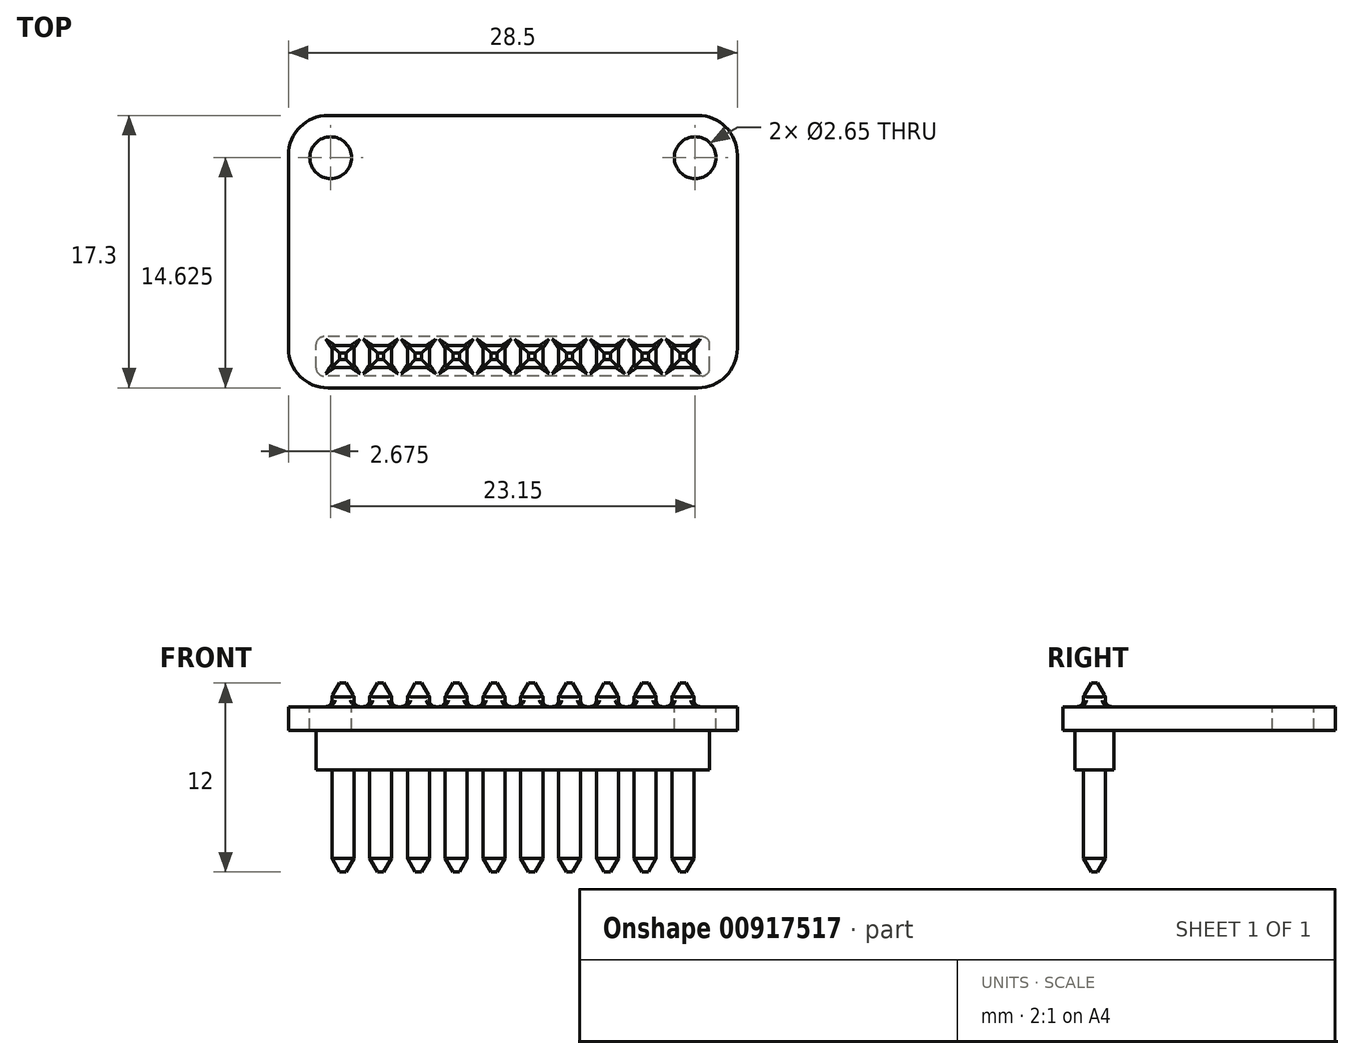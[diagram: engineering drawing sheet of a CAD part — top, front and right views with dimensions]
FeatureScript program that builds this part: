
annotation { "Feature Type Name" : "Feature", "Feature Type Description" : "" }
export const myFeature = defineFeature(function(context is Context, id is Id, definition is map)
    precondition{}
    {
        {
            var Q0;
            Q0=qCreatedBy(makeId("Top.planeOp"),FACE);
            var sketch = newSketch(context, id + "F0", { "sketchPlane" : qUnion([Q0])});
            skLineSegment(sketch, "E0.bottom", {"start": v(14.25, 8.65) * mm, "end": v(-14.25, 8.65) * mm});
            skLineSegment(sketch, "E0.top", {"start": v(14.25, -8.65) * mm, "end": v(-14.25, -8.65) * mm});
            skLineSegment(sketch, "E0.left", {"start": v(14.25, 8.65) * mm, "end": v(14.25, -8.65) * mm});
            skLineSegment(sketch, "E0.right", {"start": v(-14.25, 8.65) * mm, "end": v(-14.25, -8.65) * mm});
            skPoint(sketch, "E0.middle", {"position": v(0, 0) * mm});
            skCircle(sketch, "E1", {"center": v(-11.58, 5.97) * mm, "radius": 1.32 * mm, "construction": true});
            skLineSegment(sketch, "E2", {"start": v(0, 8.65) * mm, "end": v(0, -8.65) * mm, "construction": true});
            skCircle(sketch, "E3.MirrorC", {"center": v(11.57, 5.97) * mm, "radius": 1.32 * mm, "construction": true});
            skCircle(sketch, "E4", {"center": v(-11.58, 5.97) * mm, "radius": 1.82 * mm});
            skCircle(sketch, "E5", {"center": v(11.57, 5.97) * mm, "radius": 1.82 * mm});
            skSolve(sketch);
        }
        {
            var Q0;
            Q0 = qSketchRegion(id + "F0", true);
            extrude(context, id + "F1", {"entities" : qUnion([Q0]), "depth" : 1.5 * mm, "offsetDistance" : 25 * mm});
        }
        {
            var Q0;
            Q0=makeQuery(id+"F1.opExtrude","SWEPT_EDGE",EDGE,{"disambiguationData":[OSD([sQuery(id+"F0.wireOp",EDGE,"E0.bottom"),sQuery(id+"F0.wireOp",EDGE,"E0.left")])]});
            var Q1;
            Q1=makeQuery(id+"F1.opExtrude","SWEPT_EDGE",EDGE,{"disambiguationData":[OSD([sQuery(id+"F0.wireOp",EDGE,"E0.bottom"),sQuery(id+"F0.wireOp",EDGE,"E0.right")])]});
            var Q2;
            Q2=makeQuery(id+"F1.opExtrude","SWEPT_EDGE",EDGE,{"disambiguationData":[OSD([sQuery(id+"F0.wireOp",EDGE,"E0.top"),sQuery(id+"F0.wireOp",EDGE,"E0.right")])]});
            var Q3;
            Q3=makeQuery(id+"F1.opExtrude","SWEPT_EDGE",EDGE,{"disambiguationData":[OSD([sQuery(id+"F0.wireOp",EDGE,"E0.top"),sQuery(id+"F0.wireOp",EDGE,"E0.left")])]});
            fillet(context, id + "F2", {"entities" : qUnion([Q0, Q1, Q2, Q3]), "radius" : 2.5 * mm, "tangentPropagation" : true, "allowEdgeOverflow" : false});
        }
        {
            var Q0;
            Q0=makeQuery(id+"F1.opExtrude","CAP_FACE",FACE,{"disambiguationData":[OSD([sQuery(id+"F0.wireOp",EDGE,"E0.bottom"),sQuery(id+"F0.wireOp",EDGE,"E0.top"),sQuery(id+"F0.wireOp",EDGE,"E0.left"),sQuery(id+"F0.wireOp",EDGE,"E0.right"),sQuery(id+"F0.wireOp",EDGE,"E4"),sQuery(id+"F0.wireOp",EDGE,"E5")])],"isStart":false});
            var sketch = newSketch(context, id + "F3", { "sketchPlane" : qUnion([Q0])});
            skCircle(sketch, "E6.0", {"center": v(-11.58, 5.97) * mm, "radius": 1.83 * mm});
            skCircle(sketch, "E6.1", {"center": v(11.57, 5.97) * mm, "radius": 1.83 * mm});
            skCircle(sketch, "E7", {"center": v(-11.58, 5.97) * mm, "radius": 1.32 * mm});
            skCircle(sketch, "E8", {"center": v(11.57, 5.97) * mm, "radius": 1.32 * mm});
            skSolve(sketch);
        }
        {
            var Q0;
            Q0 = qSketchRegion(id + "F3", true);
            extrude(context, id + "F4", {"entities" : qUnion([Q0]), "operationType" : NewBodyOperationType.ADD, "oppositeDirection" : true, "depth" : 1.5 * mm, "offsetDistance" : 25 * mm});
        }
        {
            var Q0;
            Q0=makeQuery(id+"F1.opExtrude","CAP_FACE",FACE,{"disambiguationData":[OSD([sQuery(id+"F0.wireOp",EDGE,"E0.bottom"),sQuery(id+"F0.wireOp",EDGE,"E0.top"),sQuery(id+"F0.wireOp",EDGE,"E0.left"),sQuery(id+"F0.wireOp",EDGE,"E0.right"),sQuery(id+"F0.wireOp",EDGE,"E4"),sQuery(id+"F0.wireOp",EDGE,"E5")])],"isStart":true});
            var sketch = newSketch(context, id + "F5", { "sketchPlane" : qUnion([Q0])});
            skLineSegment(sketch, "E9.bottom", {"start": v(12.5, 7.9) * mm, "end": v(-12.5, 7.9) * mm});
            skLineSegment(sketch, "E9.top", {"start": v(12.5, 5.4) * mm, "end": v(-12.5, 5.4) * mm});
            skLineSegment(sketch, "E9.left", {"start": v(12.5, 7.9) * mm, "end": v(12.5, 5.4) * mm});
            skLineSegment(sketch, "E9.right", {"start": v(-12.5, 7.9) * mm, "end": v(-12.5, 5.4) * mm});
            skPoint(sketch, "E9.middle", {"position": v(0, 6.65) * mm});
            skSolve(sketch);
        }
        {
            var Q0;
            Q0 = qSketchRegion(id + "F5", true);
            extrude(context, id + "F6", {"entities" : qUnion([Q0]), "depth" : 2.5 * mm, "offsetDistance" : 25 * mm});
        }
        {
            var Q0;
            Q0=makeQuery(id+"F6.opExtrude","SWEPT_EDGE",EDGE,{"disambiguationData":[OSD([sQuery(id+"F5.wireOp",EDGE,"E9.bottom"),sQuery(id+"F5.wireOp",EDGE,"E9.left")])]});
            var Q1;
            Q1=makeQuery(id+"F6.opExtrude","SWEPT_EDGE",EDGE,{"disambiguationData":[OSD([sQuery(id+"F5.wireOp",EDGE,"E9.bottom"),sQuery(id+"F5.wireOp",EDGE,"E9.right")])]});
            var Q2;
            Q2=makeQuery(id+"F6.opExtrude","SWEPT_EDGE",EDGE,{"disambiguationData":[OSD([sQuery(id+"F5.wireOp",EDGE,"E9.top"),sQuery(id+"F5.wireOp",EDGE,"E9.right")])]});
            var Q3;
            Q3=makeQuery(id+"F6.opExtrude","SWEPT_EDGE",EDGE,{"disambiguationData":[OSD([sQuery(id+"F5.wireOp",EDGE,"E9.top"),sQuery(id+"F5.wireOp",EDGE,"E9.left")])]});
            fillet(context, id + "F7", {"entities" : qUnion([Q0, Q1, Q2, Q3]), "radius" : 0.5 * mm, "tangentPropagation" : true, "allowEdgeOverflow" : false});
        }
        {
            var Q0;
            Q0=makeQuery(id+"F6.opExtrude","CAP_FACE",FACE,{"disambiguationData":[OSD([sQuery(id+"F5.wireOp",EDGE,"E9.bottom"),sQuery(id+"F5.wireOp",EDGE,"E9.top"),sQuery(id+"F5.wireOp",EDGE,"E9.left"),sQuery(id+"F5.wireOp",EDGE,"E9.right")])],"isStart":false});
            var sketch = newSketch(context, id + "F8", { "sketchPlane" : qUnion([Q0])});
            skLineSegment(sketch, "E10.bottom", {"start": v(-10.1, 7.35) * mm, "end": v(-11.5, 7.35) * mm});
            skLineSegment(sketch, "E10.top", {"start": v(-10.1, 5.95) * mm, "end": v(-11.5, 5.95) * mm});
            skLineSegment(sketch, "E10.left", {"start": v(-10.1, 7.35) * mm, "end": v(-10.1, 5.95) * mm});
            skLineSegment(sketch, "E10.right", {"start": v(-11.5, 7.35) * mm, "end": v(-11.5, 5.95) * mm});
            skPoint(sketch, "E10.middle", {"position": v(-10.8, 6.65) * mm});
            skPoint(sketch, "E10.middle.positionSnap0", {"position": v(-12.5, 6.65) * mm});
            skPoint(sketch, "E10.centerSnap0", {"position": v(-12.5, 6.65) * mm});
            skLineSegment(sketch, "E11.1.0.0", {"start": v(-7.7, 7.35) * mm, "end": v(-7.7, 5.95) * mm});
            skLineSegment(sketch, "E11.1.0.1", {"start": v(-9.1, 7.35) * mm, "end": v(-9.1, 5.95) * mm});
            skLineSegment(sketch, "E11.1.0.2", {"start": v(-7.7, 5.95) * mm, "end": v(-9.1, 5.95) * mm});
            skPoint(sketch, "E11.1.0.3", {"position": v(-10.1, 6.65) * mm});
            skLineSegment(sketch, "E11.1.0.4", {"start": v(-7.7, 7.35) * mm, "end": v(-9.1, 7.35) * mm});
            skPoint(sketch, "E11.1.0.5", {"position": v(-8.4, 6.65) * mm});
            skPoint(sketch, "E11.1.0.6", {"position": v(-10.1, 6.65) * mm});
            skLineSegment(sketch, "E11.2.0.0", {"start": v(-5.3, 7.35) * mm, "end": v(-5.3, 5.95) * mm});
            skLineSegment(sketch, "E11.2.0.1", {"start": v(-6.7, 7.35) * mm, "end": v(-6.7, 5.95) * mm});
            skLineSegment(sketch, "E11.2.0.2", {"start": v(-5.3, 5.95) * mm, "end": v(-6.7, 5.95) * mm});
            skPoint(sketch, "E11.2.0.3", {"position": v(-7.7, 6.65) * mm});
            skLineSegment(sketch, "E11.2.0.4", {"start": v(-5.3, 7.35) * mm, "end": v(-6.7, 7.35) * mm});
            skPoint(sketch, "E11.2.0.5", {"position": v(-6, 6.65) * mm});
            skPoint(sketch, "E11.2.0.6", {"position": v(-7.7, 6.65) * mm});
            skLineSegment(sketch, "E11.3.0.0", {"start": v(-2.9, 7.35) * mm, "end": v(-2.9, 5.95) * mm});
            skLineSegment(sketch, "E11.3.0.1", {"start": v(-4.3, 7.35) * mm, "end": v(-4.3, 5.95) * mm});
            skLineSegment(sketch, "E11.3.0.2", {"start": v(-2.9, 5.95) * mm, "end": v(-4.3, 5.95) * mm});
            skPoint(sketch, "E11.3.0.3", {"position": v(-5.3, 6.65) * mm});
            skLineSegment(sketch, "E11.3.0.4", {"start": v(-2.9, 7.35) * mm, "end": v(-4.3, 7.35) * mm});
            skPoint(sketch, "E11.3.0.5", {"position": v(-3.6, 6.65) * mm});
            skPoint(sketch, "E11.3.0.6", {"position": v(-5.3, 6.65) * mm});
            skLineSegment(sketch, "E11.4.0.0", {"start": v(-0.5, 7.35) * mm, "end": v(-0.5, 5.95) * mm});
            skLineSegment(sketch, "E11.4.0.1", {"start": v(-1.9, 7.35) * mm, "end": v(-1.9, 5.95) * mm});
            skLineSegment(sketch, "E11.4.0.2", {"start": v(-0.5, 5.95) * mm, "end": v(-1.9, 5.95) * mm});
            skPoint(sketch, "E11.4.0.3", {"position": v(-2.9, 6.65) * mm});
            skLineSegment(sketch, "E11.4.0.4", {"start": v(-0.5, 7.35) * mm, "end": v(-1.9, 7.35) * mm});
            skPoint(sketch, "E11.4.0.5", {"position": v(-1.2, 6.65) * mm});
            skPoint(sketch, "E11.4.0.6", {"position": v(-2.9, 6.65) * mm});
            skLineSegment(sketch, "E11.5.0.0", {"start": v(1.9, 7.35) * mm, "end": v(1.9, 5.95) * mm});
            skLineSegment(sketch, "E11.5.0.1", {"start": v(0.5, 7.35) * mm, "end": v(0.5, 5.95) * mm});
            skLineSegment(sketch, "E11.5.0.2", {"start": v(1.9, 5.95) * mm, "end": v(0.5, 5.95) * mm});
            skPoint(sketch, "E11.5.0.3", {"position": v(-0.5, 6.65) * mm});
            skLineSegment(sketch, "E11.5.0.4", {"start": v(1.9, 7.35) * mm, "end": v(0.5, 7.35) * mm});
            skPoint(sketch, "E11.5.0.5", {"position": v(1.2, 6.65) * mm});
            skPoint(sketch, "E11.5.0.6", {"position": v(-0.5, 6.65) * mm});
            skLineSegment(sketch, "E11.6.0.0", {"start": v(4.3, 7.35) * mm, "end": v(4.3, 5.95) * mm});
            skLineSegment(sketch, "E11.6.0.1", {"start": v(2.9, 7.35) * mm, "end": v(2.9, 5.95) * mm});
            skLineSegment(sketch, "E11.6.0.2", {"start": v(4.3, 5.95) * mm, "end": v(2.9, 5.95) * mm});
            skPoint(sketch, "E11.6.0.3", {"position": v(1.9, 6.65) * mm});
            skLineSegment(sketch, "E11.6.0.4", {"start": v(4.3, 7.35) * mm, "end": v(2.9, 7.35) * mm});
            skPoint(sketch, "E11.6.0.5", {"position": v(3.6, 6.65) * mm});
            skPoint(sketch, "E11.6.0.6", {"position": v(1.9, 6.65) * mm});
            skLineSegment(sketch, "E11.7.0.0", {"start": v(6.7, 7.35) * mm, "end": v(6.7, 5.95) * mm});
            skLineSegment(sketch, "E11.7.0.1", {"start": v(5.3, 7.35) * mm, "end": v(5.3, 5.95) * mm});
            skLineSegment(sketch, "E11.7.0.2", {"start": v(6.7, 5.95) * mm, "end": v(5.3, 5.95) * mm});
            skPoint(sketch, "E11.7.0.3", {"position": v(4.3, 6.65) * mm});
            skLineSegment(sketch, "E11.7.0.4", {"start": v(6.7, 7.35) * mm, "end": v(5.3, 7.35) * mm});
            skPoint(sketch, "E11.7.0.5", {"position": v(6, 6.65) * mm});
            skPoint(sketch, "E11.7.0.6", {"position": v(4.3, 6.65) * mm});
            skLineSegment(sketch, "E11.8.0.0", {"start": v(9.1, 7.35) * mm, "end": v(9.1, 5.95) * mm});
            skLineSegment(sketch, "E11.8.0.1", {"start": v(7.7, 7.35) * mm, "end": v(7.7, 5.95) * mm});
            skLineSegment(sketch, "E11.8.0.2", {"start": v(9.1, 5.95) * mm, "end": v(7.7, 5.95) * mm});
            skPoint(sketch, "E11.8.0.3", {"position": v(6.7, 6.65) * mm});
            skLineSegment(sketch, "E11.8.0.4", {"start": v(9.1, 7.35) * mm, "end": v(7.7, 7.35) * mm});
            skPoint(sketch, "E11.8.0.5", {"position": v(8.4, 6.65) * mm});
            skPoint(sketch, "E11.8.0.6", {"position": v(6.7, 6.65) * mm});
            skLineSegment(sketch, "E11.9.0.0", {"start": v(11.5, 7.35) * mm, "end": v(11.5, 5.95) * mm});
            skLineSegment(sketch, "E11.9.0.1", {"start": v(10.1, 7.35) * mm, "end": v(10.1, 5.95) * mm});
            skLineSegment(sketch, "E11.9.0.2", {"start": v(11.5, 5.95) * mm, "end": v(10.1, 5.95) * mm});
            skPoint(sketch, "E11.9.0.3", {"position": v(9.1, 6.65) * mm});
            skLineSegment(sketch, "E11.9.0.4", {"start": v(11.5, 7.35) * mm, "end": v(10.1, 7.35) * mm});
            skPoint(sketch, "E11.9.0.5", {"position": v(10.8, 6.65) * mm});
            skPoint(sketch, "E11.9.0.6", {"position": v(9.1, 6.65) * mm});
            skLineSegment(sketch, "E11.direction1", {"start": v(-12.5, 6.65) * mm, "end": v(-10.1, 6.65) * mm, "construction": true});
            skSolve(sketch);
        }
        {
            var Q0;
            Q0 = qSketchRegion(id + "F8", true);
            extrude(context, id + "F9", {"entities" : qUnion([Q0]), "operationType" : NewBodyOperationType.ADD, "depth" : 6.5 * mm, "offsetDistance" : 25 * mm, "hasSecondDirection" : true, "secondDirectionOppositeDirection" : true, "secondDirectionDepth" : 5.5 * mm});
        }
        {
            var Q0;
            Q0=makeQuery(id+"F9.boolean.opBoolean","INTERSECT",EDGE,{"derivedFrom":[makeQuery(id+"F4.boolean.opBoolean","MERGE",FACE,{"derivedFrom":[makeQuery(id+"F1.opExtrude","CAP_FACE",FACE,{"disambiguationData":[OSD([sQuery(id+"F0.wireOp",EDGE,"E0.bottom"),sQuery(id+"F0.wireOp",EDGE,"E0.top"),sQuery(id+"F0.wireOp",EDGE,"E0.left"),sQuery(id+"F0.wireOp",EDGE,"E0.right"),sQuery(id+"F0.wireOp",EDGE,"E4"),sQuery(id+"F0.wireOp",EDGE,"E5")])],"isStart":false}),makeQuery(id+"F4.opExtrude","CAP_FACE",FACE,{"disambiguationData":[OSD([sQuery(id+"F3.wireOp",EDGE,"E6.0"),sQuery(id+"F3.wireOp",EDGE,"E7")])],"isStart":true}),makeQuery(id+"F4.opExtrude","CAP_FACE",FACE,{"disambiguationData":[OSD([sQuery(id+"F3.wireOp",EDGE,"E6.1"),sQuery(id+"F3.wireOp",EDGE,"E8")])],"isStart":true})]}),makeQuery(id+"F9.opExtrude","SWEPT_FACE",FACE,{"disambiguationData":[OSD([sQuery(id+"F8.wireOp",EDGE,"E11.9.0.0")])]})]});
            var Q1;
            Q1=makeQuery(id+"F9.boolean.opBoolean","INTERSECT",EDGE,{"derivedFrom":[makeQuery(id+"F4.boolean.opBoolean","MERGE",FACE,{"derivedFrom":[makeQuery(id+"F1.opExtrude","CAP_FACE",FACE,{"disambiguationData":[OSD([sQuery(id+"F0.wireOp",EDGE,"E0.bottom"),sQuery(id+"F0.wireOp",EDGE,"E0.top"),sQuery(id+"F0.wireOp",EDGE,"E0.left"),sQuery(id+"F0.wireOp",EDGE,"E0.right"),sQuery(id+"F0.wireOp",EDGE,"E4"),sQuery(id+"F0.wireOp",EDGE,"E5")])],"isStart":false}),makeQuery(id+"F4.opExtrude","CAP_FACE",FACE,{"disambiguationData":[OSD([sQuery(id+"F3.wireOp",EDGE,"E6.0"),sQuery(id+"F3.wireOp",EDGE,"E7")])],"isStart":true}),makeQuery(id+"F4.opExtrude","CAP_FACE",FACE,{"disambiguationData":[OSD([sQuery(id+"F3.wireOp",EDGE,"E6.1"),sQuery(id+"F3.wireOp",EDGE,"E8")])],"isStart":true})]}),makeQuery(id+"F9.opExtrude","SWEPT_FACE",FACE,{"disambiguationData":[OSD([sQuery(id+"F8.wireOp",EDGE,"E11.9.0.4")])]})]});
            var Q2;
            Q2=makeQuery(id+"F9.boolean.opBoolean","INTERSECT",EDGE,{"derivedFrom":[makeQuery(id+"F4.boolean.opBoolean","MERGE",FACE,{"derivedFrom":[makeQuery(id+"F1.opExtrude","CAP_FACE",FACE,{"disambiguationData":[OSD([sQuery(id+"F0.wireOp",EDGE,"E0.bottom"),sQuery(id+"F0.wireOp",EDGE,"E0.top"),sQuery(id+"F0.wireOp",EDGE,"E0.left"),sQuery(id+"F0.wireOp",EDGE,"E0.right"),sQuery(id+"F0.wireOp",EDGE,"E4"),sQuery(id+"F0.wireOp",EDGE,"E5")])],"isStart":false}),makeQuery(id+"F4.opExtrude","CAP_FACE",FACE,{"disambiguationData":[OSD([sQuery(id+"F3.wireOp",EDGE,"E6.0"),sQuery(id+"F3.wireOp",EDGE,"E7")])],"isStart":true}),makeQuery(id+"F4.opExtrude","CAP_FACE",FACE,{"disambiguationData":[OSD([sQuery(id+"F3.wireOp",EDGE,"E6.1"),sQuery(id+"F3.wireOp",EDGE,"E8")])],"isStart":true})]}),makeQuery(id+"F9.opExtrude","SWEPT_FACE",FACE,{"disambiguationData":[OSD([sQuery(id+"F8.wireOp",EDGE,"E11.9.0.2")])]})]});
            var Q3;
            Q3=makeQuery(id+"F9.boolean.opBoolean","INTERSECT",EDGE,{"derivedFrom":[makeQuery(id+"F4.boolean.opBoolean","MERGE",FACE,{"derivedFrom":[makeQuery(id+"F1.opExtrude","CAP_FACE",FACE,{"disambiguationData":[OSD([sQuery(id+"F0.wireOp",EDGE,"E0.bottom"),sQuery(id+"F0.wireOp",EDGE,"E0.top"),sQuery(id+"F0.wireOp",EDGE,"E0.left"),sQuery(id+"F0.wireOp",EDGE,"E0.right"),sQuery(id+"F0.wireOp",EDGE,"E4"),sQuery(id+"F0.wireOp",EDGE,"E5")])],"isStart":false}),makeQuery(id+"F4.opExtrude","CAP_FACE",FACE,{"disambiguationData":[OSD([sQuery(id+"F3.wireOp",EDGE,"E6.0"),sQuery(id+"F3.wireOp",EDGE,"E7")])],"isStart":true}),makeQuery(id+"F4.opExtrude","CAP_FACE",FACE,{"disambiguationData":[OSD([sQuery(id+"F3.wireOp",EDGE,"E6.1"),sQuery(id+"F3.wireOp",EDGE,"E8")])],"isStart":true})]}),makeQuery(id+"F9.opExtrude","SWEPT_FACE",FACE,{"disambiguationData":[OSD([sQuery(id+"F8.wireOp",EDGE,"E11.9.0.1")])]})]});
            var Q4;
            Q4=makeQuery(id+"F9.boolean.opBoolean","INTERSECT",EDGE,{"derivedFrom":[makeQuery(id+"F4.boolean.opBoolean","MERGE",FACE,{"derivedFrom":[makeQuery(id+"F1.opExtrude","CAP_FACE",FACE,{"disambiguationData":[OSD([sQuery(id+"F0.wireOp",EDGE,"E0.bottom"),sQuery(id+"F0.wireOp",EDGE,"E0.top"),sQuery(id+"F0.wireOp",EDGE,"E0.left"),sQuery(id+"F0.wireOp",EDGE,"E0.right"),sQuery(id+"F0.wireOp",EDGE,"E4"),sQuery(id+"F0.wireOp",EDGE,"E5")])],"isStart":false}),makeQuery(id+"F4.opExtrude","CAP_FACE",FACE,{"disambiguationData":[OSD([sQuery(id+"F3.wireOp",EDGE,"E6.0"),sQuery(id+"F3.wireOp",EDGE,"E7")])],"isStart":true}),makeQuery(id+"F4.opExtrude","CAP_FACE",FACE,{"disambiguationData":[OSD([sQuery(id+"F3.wireOp",EDGE,"E6.1"),sQuery(id+"F3.wireOp",EDGE,"E8")])],"isStart":true})]}),makeQuery(id+"F9.opExtrude","SWEPT_FACE",FACE,{"disambiguationData":[OSD([sQuery(id+"F8.wireOp",EDGE,"E11.8.0.4")])]})]});
            var Q5;
            Q5=makeQuery(id+"F9.boolean.opBoolean","INTERSECT",EDGE,{"derivedFrom":[makeQuery(id+"F4.boolean.opBoolean","MERGE",FACE,{"derivedFrom":[makeQuery(id+"F1.opExtrude","CAP_FACE",FACE,{"disambiguationData":[OSD([sQuery(id+"F0.wireOp",EDGE,"E0.bottom"),sQuery(id+"F0.wireOp",EDGE,"E0.top"),sQuery(id+"F0.wireOp",EDGE,"E0.left"),sQuery(id+"F0.wireOp",EDGE,"E0.right"),sQuery(id+"F0.wireOp",EDGE,"E4"),sQuery(id+"F0.wireOp",EDGE,"E5")])],"isStart":false}),makeQuery(id+"F4.opExtrude","CAP_FACE",FACE,{"disambiguationData":[OSD([sQuery(id+"F3.wireOp",EDGE,"E6.0"),sQuery(id+"F3.wireOp",EDGE,"E7")])],"isStart":true}),makeQuery(id+"F4.opExtrude","CAP_FACE",FACE,{"disambiguationData":[OSD([sQuery(id+"F3.wireOp",EDGE,"E6.1"),sQuery(id+"F3.wireOp",EDGE,"E8")])],"isStart":true})]}),makeQuery(id+"F9.opExtrude","SWEPT_FACE",FACE,{"disambiguationData":[OSD([sQuery(id+"F8.wireOp",EDGE,"E11.8.0.0")])]})]});
            var Q6;
            Q6=makeQuery(id+"F9.boolean.opBoolean","INTERSECT",EDGE,{"derivedFrom":[makeQuery(id+"F4.boolean.opBoolean","MERGE",FACE,{"derivedFrom":[makeQuery(id+"F1.opExtrude","CAP_FACE",FACE,{"disambiguationData":[OSD([sQuery(id+"F0.wireOp",EDGE,"E0.bottom"),sQuery(id+"F0.wireOp",EDGE,"E0.top"),sQuery(id+"F0.wireOp",EDGE,"E0.left"),sQuery(id+"F0.wireOp",EDGE,"E0.right"),sQuery(id+"F0.wireOp",EDGE,"E4"),sQuery(id+"F0.wireOp",EDGE,"E5")])],"isStart":false}),makeQuery(id+"F4.opExtrude","CAP_FACE",FACE,{"disambiguationData":[OSD([sQuery(id+"F3.wireOp",EDGE,"E6.0"),sQuery(id+"F3.wireOp",EDGE,"E7")])],"isStart":true}),makeQuery(id+"F4.opExtrude","CAP_FACE",FACE,{"disambiguationData":[OSD([sQuery(id+"F3.wireOp",EDGE,"E6.1"),sQuery(id+"F3.wireOp",EDGE,"E8")])],"isStart":true})]}),makeQuery(id+"F9.opExtrude","SWEPT_FACE",FACE,{"disambiguationData":[OSD([sQuery(id+"F8.wireOp",EDGE,"E11.8.0.2")])]})]});
            var Q7;
            Q7=makeQuery(id+"F9.boolean.opBoolean","INTERSECT",EDGE,{"derivedFrom":[makeQuery(id+"F4.boolean.opBoolean","MERGE",FACE,{"derivedFrom":[makeQuery(id+"F1.opExtrude","CAP_FACE",FACE,{"disambiguationData":[OSD([sQuery(id+"F0.wireOp",EDGE,"E0.bottom"),sQuery(id+"F0.wireOp",EDGE,"E0.top"),sQuery(id+"F0.wireOp",EDGE,"E0.left"),sQuery(id+"F0.wireOp",EDGE,"E0.right"),sQuery(id+"F0.wireOp",EDGE,"E4"),sQuery(id+"F0.wireOp",EDGE,"E5")])],"isStart":false}),makeQuery(id+"F4.opExtrude","CAP_FACE",FACE,{"disambiguationData":[OSD([sQuery(id+"F3.wireOp",EDGE,"E6.0"),sQuery(id+"F3.wireOp",EDGE,"E7")])],"isStart":true}),makeQuery(id+"F4.opExtrude","CAP_FACE",FACE,{"disambiguationData":[OSD([sQuery(id+"F3.wireOp",EDGE,"E6.1"),sQuery(id+"F3.wireOp",EDGE,"E8")])],"isStart":true})]}),makeQuery(id+"F9.opExtrude","SWEPT_FACE",FACE,{"disambiguationData":[OSD([sQuery(id+"F8.wireOp",EDGE,"E11.8.0.1")])]})]});
            var Q8;
            Q8=makeQuery(id+"F9.boolean.opBoolean","INTERSECT",EDGE,{"derivedFrom":[makeQuery(id+"F4.boolean.opBoolean","MERGE",FACE,{"derivedFrom":[makeQuery(id+"F1.opExtrude","CAP_FACE",FACE,{"disambiguationData":[OSD([sQuery(id+"F0.wireOp",EDGE,"E0.bottom"),sQuery(id+"F0.wireOp",EDGE,"E0.top"),sQuery(id+"F0.wireOp",EDGE,"E0.left"),sQuery(id+"F0.wireOp",EDGE,"E0.right"),sQuery(id+"F0.wireOp",EDGE,"E4"),sQuery(id+"F0.wireOp",EDGE,"E5")])],"isStart":false}),makeQuery(id+"F4.opExtrude","CAP_FACE",FACE,{"disambiguationData":[OSD([sQuery(id+"F3.wireOp",EDGE,"E6.0"),sQuery(id+"F3.wireOp",EDGE,"E7")])],"isStart":true}),makeQuery(id+"F4.opExtrude","CAP_FACE",FACE,{"disambiguationData":[OSD([sQuery(id+"F3.wireOp",EDGE,"E6.1"),sQuery(id+"F3.wireOp",EDGE,"E8")])],"isStart":true})]}),makeQuery(id+"F9.opExtrude","SWEPT_FACE",FACE,{"disambiguationData":[OSD([sQuery(id+"F8.wireOp",EDGE,"E11.7.0.0")])]})]});
            var Q9;
            Q9=makeQuery(id+"F9.boolean.opBoolean","INTERSECT",EDGE,{"derivedFrom":[makeQuery(id+"F4.boolean.opBoolean","MERGE",FACE,{"derivedFrom":[makeQuery(id+"F1.opExtrude","CAP_FACE",FACE,{"disambiguationData":[OSD([sQuery(id+"F0.wireOp",EDGE,"E0.bottom"),sQuery(id+"F0.wireOp",EDGE,"E0.top"),sQuery(id+"F0.wireOp",EDGE,"E0.left"),sQuery(id+"F0.wireOp",EDGE,"E0.right"),sQuery(id+"F0.wireOp",EDGE,"E4"),sQuery(id+"F0.wireOp",EDGE,"E5")])],"isStart":false}),makeQuery(id+"F4.opExtrude","CAP_FACE",FACE,{"disambiguationData":[OSD([sQuery(id+"F3.wireOp",EDGE,"E6.0"),sQuery(id+"F3.wireOp",EDGE,"E7")])],"isStart":true}),makeQuery(id+"F4.opExtrude","CAP_FACE",FACE,{"disambiguationData":[OSD([sQuery(id+"F3.wireOp",EDGE,"E6.1"),sQuery(id+"F3.wireOp",EDGE,"E8")])],"isStart":true})]}),makeQuery(id+"F9.opExtrude","SWEPT_FACE",FACE,{"disambiguationData":[OSD([sQuery(id+"F8.wireOp",EDGE,"E11.7.0.4")])]})]});
            var Q10;
            Q10=makeQuery(id+"F9.boolean.opBoolean","INTERSECT",EDGE,{"derivedFrom":[makeQuery(id+"F4.boolean.opBoolean","MERGE",FACE,{"derivedFrom":[makeQuery(id+"F1.opExtrude","CAP_FACE",FACE,{"disambiguationData":[OSD([sQuery(id+"F0.wireOp",EDGE,"E0.bottom"),sQuery(id+"F0.wireOp",EDGE,"E0.top"),sQuery(id+"F0.wireOp",EDGE,"E0.left"),sQuery(id+"F0.wireOp",EDGE,"E0.right"),sQuery(id+"F0.wireOp",EDGE,"E4"),sQuery(id+"F0.wireOp",EDGE,"E5")])],"isStart":false}),makeQuery(id+"F4.opExtrude","CAP_FACE",FACE,{"disambiguationData":[OSD([sQuery(id+"F3.wireOp",EDGE,"E6.0"),sQuery(id+"F3.wireOp",EDGE,"E7")])],"isStart":true}),makeQuery(id+"F4.opExtrude","CAP_FACE",FACE,{"disambiguationData":[OSD([sQuery(id+"F3.wireOp",EDGE,"E6.1"),sQuery(id+"F3.wireOp",EDGE,"E8")])],"isStart":true})]}),makeQuery(id+"F9.opExtrude","SWEPT_FACE",FACE,{"disambiguationData":[OSD([sQuery(id+"F8.wireOp",EDGE,"E11.7.0.2")])]})]});
            var Q11;
            Q11=makeQuery(id+"F9.boolean.opBoolean","INTERSECT",EDGE,{"derivedFrom":[makeQuery(id+"F4.boolean.opBoolean","MERGE",FACE,{"derivedFrom":[makeQuery(id+"F1.opExtrude","CAP_FACE",FACE,{"disambiguationData":[OSD([sQuery(id+"F0.wireOp",EDGE,"E0.bottom"),sQuery(id+"F0.wireOp",EDGE,"E0.top"),sQuery(id+"F0.wireOp",EDGE,"E0.left"),sQuery(id+"F0.wireOp",EDGE,"E0.right"),sQuery(id+"F0.wireOp",EDGE,"E4"),sQuery(id+"F0.wireOp",EDGE,"E5")])],"isStart":false}),makeQuery(id+"F4.opExtrude","CAP_FACE",FACE,{"disambiguationData":[OSD([sQuery(id+"F3.wireOp",EDGE,"E6.0"),sQuery(id+"F3.wireOp",EDGE,"E7")])],"isStart":true}),makeQuery(id+"F4.opExtrude","CAP_FACE",FACE,{"disambiguationData":[OSD([sQuery(id+"F3.wireOp",EDGE,"E6.1"),sQuery(id+"F3.wireOp",EDGE,"E8")])],"isStart":true})]}),makeQuery(id+"F9.opExtrude","SWEPT_FACE",FACE,{"disambiguationData":[OSD([sQuery(id+"F8.wireOp",EDGE,"E11.7.0.1")])]})]});
            var Q12;
            Q12=makeQuery(id+"F9.boolean.opBoolean","INTERSECT",EDGE,{"derivedFrom":[makeQuery(id+"F4.boolean.opBoolean","MERGE",FACE,{"derivedFrom":[makeQuery(id+"F1.opExtrude","CAP_FACE",FACE,{"disambiguationData":[OSD([sQuery(id+"F0.wireOp",EDGE,"E0.bottom"),sQuery(id+"F0.wireOp",EDGE,"E0.top"),sQuery(id+"F0.wireOp",EDGE,"E0.left"),sQuery(id+"F0.wireOp",EDGE,"E0.right"),sQuery(id+"F0.wireOp",EDGE,"E4"),sQuery(id+"F0.wireOp",EDGE,"E5")])],"isStart":false}),makeQuery(id+"F4.opExtrude","CAP_FACE",FACE,{"disambiguationData":[OSD([sQuery(id+"F3.wireOp",EDGE,"E6.0"),sQuery(id+"F3.wireOp",EDGE,"E7")])],"isStart":true}),makeQuery(id+"F4.opExtrude","CAP_FACE",FACE,{"disambiguationData":[OSD([sQuery(id+"F3.wireOp",EDGE,"E6.1"),sQuery(id+"F3.wireOp",EDGE,"E8")])],"isStart":true})]}),makeQuery(id+"F9.opExtrude","SWEPT_FACE",FACE,{"disambiguationData":[OSD([sQuery(id+"F8.wireOp",EDGE,"E11.6.0.0")])]})]});
            var Q13;
            Q13=makeQuery(id+"F9.boolean.opBoolean","INTERSECT",EDGE,{"derivedFrom":[makeQuery(id+"F4.boolean.opBoolean","MERGE",FACE,{"derivedFrom":[makeQuery(id+"F1.opExtrude","CAP_FACE",FACE,{"disambiguationData":[OSD([sQuery(id+"F0.wireOp",EDGE,"E0.bottom"),sQuery(id+"F0.wireOp",EDGE,"E0.top"),sQuery(id+"F0.wireOp",EDGE,"E0.left"),sQuery(id+"F0.wireOp",EDGE,"E0.right"),sQuery(id+"F0.wireOp",EDGE,"E4"),sQuery(id+"F0.wireOp",EDGE,"E5")])],"isStart":false}),makeQuery(id+"F4.opExtrude","CAP_FACE",FACE,{"disambiguationData":[OSD([sQuery(id+"F3.wireOp",EDGE,"E6.0"),sQuery(id+"F3.wireOp",EDGE,"E7")])],"isStart":true}),makeQuery(id+"F4.opExtrude","CAP_FACE",FACE,{"disambiguationData":[OSD([sQuery(id+"F3.wireOp",EDGE,"E6.1"),sQuery(id+"F3.wireOp",EDGE,"E8")])],"isStart":true})]}),makeQuery(id+"F9.opExtrude","SWEPT_FACE",FACE,{"disambiguationData":[OSD([sQuery(id+"F8.wireOp",EDGE,"E11.6.0.4")])]})]});
            var Q14;
            Q14=makeQuery(id+"F9.boolean.opBoolean","INTERSECT",EDGE,{"derivedFrom":[makeQuery(id+"F4.boolean.opBoolean","MERGE",FACE,{"derivedFrom":[makeQuery(id+"F1.opExtrude","CAP_FACE",FACE,{"disambiguationData":[OSD([sQuery(id+"F0.wireOp",EDGE,"E0.bottom"),sQuery(id+"F0.wireOp",EDGE,"E0.top"),sQuery(id+"F0.wireOp",EDGE,"E0.left"),sQuery(id+"F0.wireOp",EDGE,"E0.right"),sQuery(id+"F0.wireOp",EDGE,"E4"),sQuery(id+"F0.wireOp",EDGE,"E5")])],"isStart":false}),makeQuery(id+"F4.opExtrude","CAP_FACE",FACE,{"disambiguationData":[OSD([sQuery(id+"F3.wireOp",EDGE,"E6.0"),sQuery(id+"F3.wireOp",EDGE,"E7")])],"isStart":true}),makeQuery(id+"F4.opExtrude","CAP_FACE",FACE,{"disambiguationData":[OSD([sQuery(id+"F3.wireOp",EDGE,"E6.1"),sQuery(id+"F3.wireOp",EDGE,"E8")])],"isStart":true})]}),makeQuery(id+"F9.opExtrude","SWEPT_FACE",FACE,{"disambiguationData":[OSD([sQuery(id+"F8.wireOp",EDGE,"E11.6.0.2")])]})]});
            var Q15;
            Q15=makeQuery(id+"F9.boolean.opBoolean","INTERSECT",EDGE,{"derivedFrom":[makeQuery(id+"F4.boolean.opBoolean","MERGE",FACE,{"derivedFrom":[makeQuery(id+"F1.opExtrude","CAP_FACE",FACE,{"disambiguationData":[OSD([sQuery(id+"F0.wireOp",EDGE,"E0.bottom"),sQuery(id+"F0.wireOp",EDGE,"E0.top"),sQuery(id+"F0.wireOp",EDGE,"E0.left"),sQuery(id+"F0.wireOp",EDGE,"E0.right"),sQuery(id+"F0.wireOp",EDGE,"E4"),sQuery(id+"F0.wireOp",EDGE,"E5")])],"isStart":false}),makeQuery(id+"F4.opExtrude","CAP_FACE",FACE,{"disambiguationData":[OSD([sQuery(id+"F3.wireOp",EDGE,"E6.0"),sQuery(id+"F3.wireOp",EDGE,"E7")])],"isStart":true}),makeQuery(id+"F4.opExtrude","CAP_FACE",FACE,{"disambiguationData":[OSD([sQuery(id+"F3.wireOp",EDGE,"E6.1"),sQuery(id+"F3.wireOp",EDGE,"E8")])],"isStart":true})]}),makeQuery(id+"F9.opExtrude","SWEPT_FACE",FACE,{"disambiguationData":[OSD([sQuery(id+"F8.wireOp",EDGE,"E11.6.0.1")])]})]});
            var Q16;
            Q16=makeQuery(id+"F9.boolean.opBoolean","INTERSECT",EDGE,{"derivedFrom":[makeQuery(id+"F4.boolean.opBoolean","MERGE",FACE,{"derivedFrom":[makeQuery(id+"F1.opExtrude","CAP_FACE",FACE,{"disambiguationData":[OSD([sQuery(id+"F0.wireOp",EDGE,"E0.bottom"),sQuery(id+"F0.wireOp",EDGE,"E0.top"),sQuery(id+"F0.wireOp",EDGE,"E0.left"),sQuery(id+"F0.wireOp",EDGE,"E0.right"),sQuery(id+"F0.wireOp",EDGE,"E4"),sQuery(id+"F0.wireOp",EDGE,"E5")])],"isStart":false}),makeQuery(id+"F4.opExtrude","CAP_FACE",FACE,{"disambiguationData":[OSD([sQuery(id+"F3.wireOp",EDGE,"E6.0"),sQuery(id+"F3.wireOp",EDGE,"E7")])],"isStart":true}),makeQuery(id+"F4.opExtrude","CAP_FACE",FACE,{"disambiguationData":[OSD([sQuery(id+"F3.wireOp",EDGE,"E6.1"),sQuery(id+"F3.wireOp",EDGE,"E8")])],"isStart":true})]}),makeQuery(id+"F9.opExtrude","SWEPT_FACE",FACE,{"disambiguationData":[OSD([sQuery(id+"F8.wireOp",EDGE,"E11.5.0.2")])]})]});
            var Q17;
            Q17=makeQuery(id+"F9.boolean.opBoolean","INTERSECT",EDGE,{"derivedFrom":[makeQuery(id+"F4.boolean.opBoolean","MERGE",FACE,{"derivedFrom":[makeQuery(id+"F1.opExtrude","CAP_FACE",FACE,{"disambiguationData":[OSD([sQuery(id+"F0.wireOp",EDGE,"E0.bottom"),sQuery(id+"F0.wireOp",EDGE,"E0.top"),sQuery(id+"F0.wireOp",EDGE,"E0.left"),sQuery(id+"F0.wireOp",EDGE,"E0.right"),sQuery(id+"F0.wireOp",EDGE,"E4"),sQuery(id+"F0.wireOp",EDGE,"E5")])],"isStart":false}),makeQuery(id+"F4.opExtrude","CAP_FACE",FACE,{"disambiguationData":[OSD([sQuery(id+"F3.wireOp",EDGE,"E6.0"),sQuery(id+"F3.wireOp",EDGE,"E7")])],"isStart":true}),makeQuery(id+"F4.opExtrude","CAP_FACE",FACE,{"disambiguationData":[OSD([sQuery(id+"F3.wireOp",EDGE,"E6.1"),sQuery(id+"F3.wireOp",EDGE,"E8")])],"isStart":true})]}),makeQuery(id+"F9.opExtrude","SWEPT_FACE",FACE,{"disambiguationData":[OSD([sQuery(id+"F8.wireOp",EDGE,"E11.5.0.1")])]})]});
            var Q18;
            Q18=makeQuery(id+"F9.boolean.opBoolean","INTERSECT",EDGE,{"derivedFrom":[makeQuery(id+"F4.boolean.opBoolean","MERGE",FACE,{"derivedFrom":[makeQuery(id+"F1.opExtrude","CAP_FACE",FACE,{"disambiguationData":[OSD([sQuery(id+"F0.wireOp",EDGE,"E0.bottom"),sQuery(id+"F0.wireOp",EDGE,"E0.top"),sQuery(id+"F0.wireOp",EDGE,"E0.left"),sQuery(id+"F0.wireOp",EDGE,"E0.right"),sQuery(id+"F0.wireOp",EDGE,"E4"),sQuery(id+"F0.wireOp",EDGE,"E5")])],"isStart":false}),makeQuery(id+"F4.opExtrude","CAP_FACE",FACE,{"disambiguationData":[OSD([sQuery(id+"F3.wireOp",EDGE,"E6.0"),sQuery(id+"F3.wireOp",EDGE,"E7")])],"isStart":true}),makeQuery(id+"F4.opExtrude","CAP_FACE",FACE,{"disambiguationData":[OSD([sQuery(id+"F3.wireOp",EDGE,"E6.1"),sQuery(id+"F3.wireOp",EDGE,"E8")])],"isStart":true})]}),makeQuery(id+"F9.opExtrude","SWEPT_FACE",FACE,{"disambiguationData":[OSD([sQuery(id+"F8.wireOp",EDGE,"E11.5.0.0")])]})]});
            var Q19;
            Q19=makeQuery(id+"F9.boolean.opBoolean","INTERSECT",EDGE,{"derivedFrom":[makeQuery(id+"F4.boolean.opBoolean","MERGE",FACE,{"derivedFrom":[makeQuery(id+"F1.opExtrude","CAP_FACE",FACE,{"disambiguationData":[OSD([sQuery(id+"F0.wireOp",EDGE,"E0.bottom"),sQuery(id+"F0.wireOp",EDGE,"E0.top"),sQuery(id+"F0.wireOp",EDGE,"E0.left"),sQuery(id+"F0.wireOp",EDGE,"E0.right"),sQuery(id+"F0.wireOp",EDGE,"E4"),sQuery(id+"F0.wireOp",EDGE,"E5")])],"isStart":false}),makeQuery(id+"F4.opExtrude","CAP_FACE",FACE,{"disambiguationData":[OSD([sQuery(id+"F3.wireOp",EDGE,"E6.0"),sQuery(id+"F3.wireOp",EDGE,"E7")])],"isStart":true}),makeQuery(id+"F4.opExtrude","CAP_FACE",FACE,{"disambiguationData":[OSD([sQuery(id+"F3.wireOp",EDGE,"E6.1"),sQuery(id+"F3.wireOp",EDGE,"E8")])],"isStart":true})]}),makeQuery(id+"F9.opExtrude","SWEPT_FACE",FACE,{"disambiguationData":[OSD([sQuery(id+"F8.wireOp",EDGE,"E11.5.0.4")])]})]});
            var Q20;
            Q20=makeQuery(id+"F9.boolean.opBoolean","INTERSECT",EDGE,{"derivedFrom":[makeQuery(id+"F4.boolean.opBoolean","MERGE",FACE,{"derivedFrom":[makeQuery(id+"F1.opExtrude","CAP_FACE",FACE,{"disambiguationData":[OSD([sQuery(id+"F0.wireOp",EDGE,"E0.bottom"),sQuery(id+"F0.wireOp",EDGE,"E0.top"),sQuery(id+"F0.wireOp",EDGE,"E0.left"),sQuery(id+"F0.wireOp",EDGE,"E0.right"),sQuery(id+"F0.wireOp",EDGE,"E4"),sQuery(id+"F0.wireOp",EDGE,"E5")])],"isStart":false}),makeQuery(id+"F4.opExtrude","CAP_FACE",FACE,{"disambiguationData":[OSD([sQuery(id+"F3.wireOp",EDGE,"E6.0"),sQuery(id+"F3.wireOp",EDGE,"E7")])],"isStart":true}),makeQuery(id+"F4.opExtrude","CAP_FACE",FACE,{"disambiguationData":[OSD([sQuery(id+"F3.wireOp",EDGE,"E6.1"),sQuery(id+"F3.wireOp",EDGE,"E8")])],"isStart":true})]}),makeQuery(id+"F9.opExtrude","SWEPT_FACE",FACE,{"disambiguationData":[OSD([sQuery(id+"F8.wireOp",EDGE,"E11.3.0.0")])]})]});
            var Q21;
            Q21=makeQuery(id+"F9.boolean.opBoolean","INTERSECT",EDGE,{"derivedFrom":[makeQuery(id+"F4.boolean.opBoolean","MERGE",FACE,{"derivedFrom":[makeQuery(id+"F1.opExtrude","CAP_FACE",FACE,{"disambiguationData":[OSD([sQuery(id+"F0.wireOp",EDGE,"E0.bottom"),sQuery(id+"F0.wireOp",EDGE,"E0.top"),sQuery(id+"F0.wireOp",EDGE,"E0.left"),sQuery(id+"F0.wireOp",EDGE,"E0.right"),sQuery(id+"F0.wireOp",EDGE,"E4"),sQuery(id+"F0.wireOp",EDGE,"E5")])],"isStart":false}),makeQuery(id+"F4.opExtrude","CAP_FACE",FACE,{"disambiguationData":[OSD([sQuery(id+"F3.wireOp",EDGE,"E6.0"),sQuery(id+"F3.wireOp",EDGE,"E7")])],"isStart":true}),makeQuery(id+"F4.opExtrude","CAP_FACE",FACE,{"disambiguationData":[OSD([sQuery(id+"F3.wireOp",EDGE,"E6.1"),sQuery(id+"F3.wireOp",EDGE,"E8")])],"isStart":true})]}),makeQuery(id+"F9.opExtrude","SWEPT_FACE",FACE,{"disambiguationData":[OSD([sQuery(id+"F8.wireOp",EDGE,"E11.4.0.4")])]})]});
            var Q22;
            Q22=makeQuery(id+"F9.boolean.opBoolean","INTERSECT",EDGE,{"derivedFrom":[makeQuery(id+"F4.boolean.opBoolean","MERGE",FACE,{"derivedFrom":[makeQuery(id+"F1.opExtrude","CAP_FACE",FACE,{"disambiguationData":[OSD([sQuery(id+"F0.wireOp",EDGE,"E0.bottom"),sQuery(id+"F0.wireOp",EDGE,"E0.top"),sQuery(id+"F0.wireOp",EDGE,"E0.left"),sQuery(id+"F0.wireOp",EDGE,"E0.right"),sQuery(id+"F0.wireOp",EDGE,"E4"),sQuery(id+"F0.wireOp",EDGE,"E5")])],"isStart":false}),makeQuery(id+"F4.opExtrude","CAP_FACE",FACE,{"disambiguationData":[OSD([sQuery(id+"F3.wireOp",EDGE,"E6.0"),sQuery(id+"F3.wireOp",EDGE,"E7")])],"isStart":true}),makeQuery(id+"F4.opExtrude","CAP_FACE",FACE,{"disambiguationData":[OSD([sQuery(id+"F3.wireOp",EDGE,"E6.1"),sQuery(id+"F3.wireOp",EDGE,"E8")])],"isStart":true})]}),makeQuery(id+"F9.opExtrude","SWEPT_FACE",FACE,{"disambiguationData":[OSD([sQuery(id+"F8.wireOp",EDGE,"E11.4.0.0")])]})]});
            var Q23;
            Q23=makeQuery(id+"F9.boolean.opBoolean","INTERSECT",EDGE,{"derivedFrom":[makeQuery(id+"F4.boolean.opBoolean","MERGE",FACE,{"derivedFrom":[makeQuery(id+"F1.opExtrude","CAP_FACE",FACE,{"disambiguationData":[OSD([sQuery(id+"F0.wireOp",EDGE,"E0.bottom"),sQuery(id+"F0.wireOp",EDGE,"E0.top"),sQuery(id+"F0.wireOp",EDGE,"E0.left"),sQuery(id+"F0.wireOp",EDGE,"E0.right"),sQuery(id+"F0.wireOp",EDGE,"E4"),sQuery(id+"F0.wireOp",EDGE,"E5")])],"isStart":false}),makeQuery(id+"F4.opExtrude","CAP_FACE",FACE,{"disambiguationData":[OSD([sQuery(id+"F3.wireOp",EDGE,"E6.0"),sQuery(id+"F3.wireOp",EDGE,"E7")])],"isStart":true}),makeQuery(id+"F4.opExtrude","CAP_FACE",FACE,{"disambiguationData":[OSD([sQuery(id+"F3.wireOp",EDGE,"E6.1"),sQuery(id+"F3.wireOp",EDGE,"E8")])],"isStart":true})]}),makeQuery(id+"F9.opExtrude","SWEPT_FACE",FACE,{"disambiguationData":[OSD([sQuery(id+"F8.wireOp",EDGE,"E11.3.0.4")])]})]});
            var Q24;
            Q24=makeQuery(id+"F9.boolean.opBoolean","INTERSECT",EDGE,{"derivedFrom":[makeQuery(id+"F4.boolean.opBoolean","MERGE",FACE,{"derivedFrom":[makeQuery(id+"F1.opExtrude","CAP_FACE",FACE,{"disambiguationData":[OSD([sQuery(id+"F0.wireOp",EDGE,"E0.bottom"),sQuery(id+"F0.wireOp",EDGE,"E0.top"),sQuery(id+"F0.wireOp",EDGE,"E0.left"),sQuery(id+"F0.wireOp",EDGE,"E0.right"),sQuery(id+"F0.wireOp",EDGE,"E4"),sQuery(id+"F0.wireOp",EDGE,"E5")])],"isStart":false}),makeQuery(id+"F4.opExtrude","CAP_FACE",FACE,{"disambiguationData":[OSD([sQuery(id+"F3.wireOp",EDGE,"E6.0"),sQuery(id+"F3.wireOp",EDGE,"E7")])],"isStart":true}),makeQuery(id+"F4.opExtrude","CAP_FACE",FACE,{"disambiguationData":[OSD([sQuery(id+"F3.wireOp",EDGE,"E6.1"),sQuery(id+"F3.wireOp",EDGE,"E8")])],"isStart":true})]}),makeQuery(id+"F9.opExtrude","SWEPT_FACE",FACE,{"disambiguationData":[OSD([sQuery(id+"F8.wireOp",EDGE,"E11.3.0.2")])]})]});
            var Q25;
            Q25=makeQuery(id+"F9.boolean.opBoolean","INTERSECT",EDGE,{"derivedFrom":[makeQuery(id+"F4.boolean.opBoolean","MERGE",FACE,{"derivedFrom":[makeQuery(id+"F1.opExtrude","CAP_FACE",FACE,{"disambiguationData":[OSD([sQuery(id+"F0.wireOp",EDGE,"E0.bottom"),sQuery(id+"F0.wireOp",EDGE,"E0.top"),sQuery(id+"F0.wireOp",EDGE,"E0.left"),sQuery(id+"F0.wireOp",EDGE,"E0.right"),sQuery(id+"F0.wireOp",EDGE,"E4"),sQuery(id+"F0.wireOp",EDGE,"E5")])],"isStart":false}),makeQuery(id+"F4.opExtrude","CAP_FACE",FACE,{"disambiguationData":[OSD([sQuery(id+"F3.wireOp",EDGE,"E6.0"),sQuery(id+"F3.wireOp",EDGE,"E7")])],"isStart":true}),makeQuery(id+"F4.opExtrude","CAP_FACE",FACE,{"disambiguationData":[OSD([sQuery(id+"F3.wireOp",EDGE,"E6.1"),sQuery(id+"F3.wireOp",EDGE,"E8")])],"isStart":true})]}),makeQuery(id+"F9.opExtrude","SWEPT_FACE",FACE,{"disambiguationData":[OSD([sQuery(id+"F8.wireOp",EDGE,"E11.4.0.2")])]})]});
            var Q26;
            Q26=makeQuery(id+"F9.boolean.opBoolean","INTERSECT",EDGE,{"derivedFrom":[makeQuery(id+"F4.boolean.opBoolean","MERGE",FACE,{"derivedFrom":[makeQuery(id+"F1.opExtrude","CAP_FACE",FACE,{"disambiguationData":[OSD([sQuery(id+"F0.wireOp",EDGE,"E0.bottom"),sQuery(id+"F0.wireOp",EDGE,"E0.top"),sQuery(id+"F0.wireOp",EDGE,"E0.left"),sQuery(id+"F0.wireOp",EDGE,"E0.right"),sQuery(id+"F0.wireOp",EDGE,"E4"),sQuery(id+"F0.wireOp",EDGE,"E5")])],"isStart":false}),makeQuery(id+"F4.opExtrude","CAP_FACE",FACE,{"disambiguationData":[OSD([sQuery(id+"F3.wireOp",EDGE,"E6.0"),sQuery(id+"F3.wireOp",EDGE,"E7")])],"isStart":true}),makeQuery(id+"F4.opExtrude","CAP_FACE",FACE,{"disambiguationData":[OSD([sQuery(id+"F3.wireOp",EDGE,"E6.1"),sQuery(id+"F3.wireOp",EDGE,"E8")])],"isStart":true})]}),makeQuery(id+"F9.opExtrude","SWEPT_FACE",FACE,{"disambiguationData":[OSD([sQuery(id+"F8.wireOp",EDGE,"E11.2.0.2")])]})]});
            var Q27;
            Q27=makeQuery(id+"F9.boolean.opBoolean","INTERSECT",EDGE,{"derivedFrom":[makeQuery(id+"F4.boolean.opBoolean","MERGE",FACE,{"derivedFrom":[makeQuery(id+"F1.opExtrude","CAP_FACE",FACE,{"disambiguationData":[OSD([sQuery(id+"F0.wireOp",EDGE,"E0.bottom"),sQuery(id+"F0.wireOp",EDGE,"E0.top"),sQuery(id+"F0.wireOp",EDGE,"E0.left"),sQuery(id+"F0.wireOp",EDGE,"E0.right"),sQuery(id+"F0.wireOp",EDGE,"E4"),sQuery(id+"F0.wireOp",EDGE,"E5")])],"isStart":false}),makeQuery(id+"F4.opExtrude","CAP_FACE",FACE,{"disambiguationData":[OSD([sQuery(id+"F3.wireOp",EDGE,"E6.0"),sQuery(id+"F3.wireOp",EDGE,"E7")])],"isStart":true}),makeQuery(id+"F4.opExtrude","CAP_FACE",FACE,{"disambiguationData":[OSD([sQuery(id+"F3.wireOp",EDGE,"E6.1"),sQuery(id+"F3.wireOp",EDGE,"E8")])],"isStart":true})]}),makeQuery(id+"F9.opExtrude","SWEPT_FACE",FACE,{"disambiguationData":[OSD([sQuery(id+"F8.wireOp",EDGE,"E11.1.0.2")])]})]});
            var Q28;
            Q28=makeQuery(id+"F9.boolean.opBoolean","INTERSECT",EDGE,{"derivedFrom":[makeQuery(id+"F4.boolean.opBoolean","MERGE",FACE,{"derivedFrom":[makeQuery(id+"F1.opExtrude","CAP_FACE",FACE,{"disambiguationData":[OSD([sQuery(id+"F0.wireOp",EDGE,"E0.bottom"),sQuery(id+"F0.wireOp",EDGE,"E0.top"),sQuery(id+"F0.wireOp",EDGE,"E0.left"),sQuery(id+"F0.wireOp",EDGE,"E0.right"),sQuery(id+"F0.wireOp",EDGE,"E4"),sQuery(id+"F0.wireOp",EDGE,"E5")])],"isStart":false}),makeQuery(id+"F4.opExtrude","CAP_FACE",FACE,{"disambiguationData":[OSD([sQuery(id+"F3.wireOp",EDGE,"E6.0"),sQuery(id+"F3.wireOp",EDGE,"E7")])],"isStart":true}),makeQuery(id+"F4.opExtrude","CAP_FACE",FACE,{"disambiguationData":[OSD([sQuery(id+"F3.wireOp",EDGE,"E6.1"),sQuery(id+"F3.wireOp",EDGE,"E8")])],"isStart":true})]}),makeQuery(id+"F9.opExtrude","SWEPT_FACE",FACE,{"disambiguationData":[OSD([sQuery(id+"F8.wireOp",EDGE,"E10.top")])]})]});
            var Q29;
            Q29=makeQuery(id+"F9.boolean.opBoolean","INTERSECT",EDGE,{"derivedFrom":[makeQuery(id+"F4.boolean.opBoolean","MERGE",FACE,{"derivedFrom":[makeQuery(id+"F1.opExtrude","CAP_FACE",FACE,{"disambiguationData":[OSD([sQuery(id+"F0.wireOp",EDGE,"E0.bottom"),sQuery(id+"F0.wireOp",EDGE,"E0.top"),sQuery(id+"F0.wireOp",EDGE,"E0.left"),sQuery(id+"F0.wireOp",EDGE,"E0.right"),sQuery(id+"F0.wireOp",EDGE,"E4"),sQuery(id+"F0.wireOp",EDGE,"E5")])],"isStart":false}),makeQuery(id+"F4.opExtrude","CAP_FACE",FACE,{"disambiguationData":[OSD([sQuery(id+"F3.wireOp",EDGE,"E6.0"),sQuery(id+"F3.wireOp",EDGE,"E7")])],"isStart":true}),makeQuery(id+"F4.opExtrude","CAP_FACE",FACE,{"disambiguationData":[OSD([sQuery(id+"F3.wireOp",EDGE,"E6.1"),sQuery(id+"F3.wireOp",EDGE,"E8")])],"isStart":true})]}),makeQuery(id+"F9.opExtrude","SWEPT_FACE",FACE,{"disambiguationData":[OSD([sQuery(id+"F8.wireOp",EDGE,"E10.left")])]})]});
            var Q30;
            Q30=makeQuery(id+"F9.boolean.opBoolean","INTERSECT",EDGE,{"derivedFrom":[makeQuery(id+"F4.boolean.opBoolean","MERGE",FACE,{"derivedFrom":[makeQuery(id+"F1.opExtrude","CAP_FACE",FACE,{"disambiguationData":[OSD([sQuery(id+"F0.wireOp",EDGE,"E0.bottom"),sQuery(id+"F0.wireOp",EDGE,"E0.top"),sQuery(id+"F0.wireOp",EDGE,"E0.left"),sQuery(id+"F0.wireOp",EDGE,"E0.right"),sQuery(id+"F0.wireOp",EDGE,"E4"),sQuery(id+"F0.wireOp",EDGE,"E5")])],"isStart":false}),makeQuery(id+"F4.opExtrude","CAP_FACE",FACE,{"disambiguationData":[OSD([sQuery(id+"F3.wireOp",EDGE,"E6.0"),sQuery(id+"F3.wireOp",EDGE,"E7")])],"isStart":true}),makeQuery(id+"F4.opExtrude","CAP_FACE",FACE,{"disambiguationData":[OSD([sQuery(id+"F3.wireOp",EDGE,"E6.1"),sQuery(id+"F3.wireOp",EDGE,"E8")])],"isStart":true})]}),makeQuery(id+"F9.opExtrude","SWEPT_FACE",FACE,{"disambiguationData":[OSD([sQuery(id+"F8.wireOp",EDGE,"E11.1.0.0")])]})]});
            var Q31;
            Q31=makeQuery(id+"F9.boolean.opBoolean","INTERSECT",EDGE,{"derivedFrom":[makeQuery(id+"F4.boolean.opBoolean","MERGE",FACE,{"derivedFrom":[makeQuery(id+"F1.opExtrude","CAP_FACE",FACE,{"disambiguationData":[OSD([sQuery(id+"F0.wireOp",EDGE,"E0.bottom"),sQuery(id+"F0.wireOp",EDGE,"E0.top"),sQuery(id+"F0.wireOp",EDGE,"E0.left"),sQuery(id+"F0.wireOp",EDGE,"E0.right"),sQuery(id+"F0.wireOp",EDGE,"E4"),sQuery(id+"F0.wireOp",EDGE,"E5")])],"isStart":false}),makeQuery(id+"F4.opExtrude","CAP_FACE",FACE,{"disambiguationData":[OSD([sQuery(id+"F3.wireOp",EDGE,"E6.0"),sQuery(id+"F3.wireOp",EDGE,"E7")])],"isStart":true}),makeQuery(id+"F4.opExtrude","CAP_FACE",FACE,{"disambiguationData":[OSD([sQuery(id+"F3.wireOp",EDGE,"E6.1"),sQuery(id+"F3.wireOp",EDGE,"E8")])],"isStart":true})]}),makeQuery(id+"F9.opExtrude","SWEPT_FACE",FACE,{"disambiguationData":[OSD([sQuery(id+"F8.wireOp",EDGE,"E11.2.0.0")])]})]});
            var Q32;
            Q32=makeQuery(id+"F9.boolean.opBoolean","INTERSECT",EDGE,{"derivedFrom":[makeQuery(id+"F4.boolean.opBoolean","MERGE",FACE,{"derivedFrom":[makeQuery(id+"F1.opExtrude","CAP_FACE",FACE,{"disambiguationData":[OSD([sQuery(id+"F0.wireOp",EDGE,"E0.bottom"),sQuery(id+"F0.wireOp",EDGE,"E0.top"),sQuery(id+"F0.wireOp",EDGE,"E0.left"),sQuery(id+"F0.wireOp",EDGE,"E0.right"),sQuery(id+"F0.wireOp",EDGE,"E4"),sQuery(id+"F0.wireOp",EDGE,"E5")])],"isStart":false}),makeQuery(id+"F4.opExtrude","CAP_FACE",FACE,{"disambiguationData":[OSD([sQuery(id+"F3.wireOp",EDGE,"E6.0"),sQuery(id+"F3.wireOp",EDGE,"E7")])],"isStart":true}),makeQuery(id+"F4.opExtrude","CAP_FACE",FACE,{"disambiguationData":[OSD([sQuery(id+"F3.wireOp",EDGE,"E6.1"),sQuery(id+"F3.wireOp",EDGE,"E8")])],"isStart":true})]}),makeQuery(id+"F9.opExtrude","SWEPT_FACE",FACE,{"disambiguationData":[OSD([sQuery(id+"F8.wireOp",EDGE,"E11.4.0.1")])]})]});
            var Q33;
            Q33=makeQuery(id+"F9.boolean.opBoolean","INTERSECT",EDGE,{"derivedFrom":[makeQuery(id+"F4.boolean.opBoolean","MERGE",FACE,{"derivedFrom":[makeQuery(id+"F1.opExtrude","CAP_FACE",FACE,{"disambiguationData":[OSD([sQuery(id+"F0.wireOp",EDGE,"E0.bottom"),sQuery(id+"F0.wireOp",EDGE,"E0.top"),sQuery(id+"F0.wireOp",EDGE,"E0.left"),sQuery(id+"F0.wireOp",EDGE,"E0.right"),sQuery(id+"F0.wireOp",EDGE,"E4"),sQuery(id+"F0.wireOp",EDGE,"E5")])],"isStart":false}),makeQuery(id+"F4.opExtrude","CAP_FACE",FACE,{"disambiguationData":[OSD([sQuery(id+"F3.wireOp",EDGE,"E6.0"),sQuery(id+"F3.wireOp",EDGE,"E7")])],"isStart":true}),makeQuery(id+"F4.opExtrude","CAP_FACE",FACE,{"disambiguationData":[OSD([sQuery(id+"F3.wireOp",EDGE,"E6.1"),sQuery(id+"F3.wireOp",EDGE,"E8")])],"isStart":true})]}),makeQuery(id+"F9.opExtrude","SWEPT_FACE",FACE,{"disambiguationData":[OSD([sQuery(id+"F8.wireOp",EDGE,"E11.3.0.1")])]})]});
            var Q34;
            Q34=makeQuery(id+"F9.boolean.opBoolean","INTERSECT",EDGE,{"derivedFrom":[makeQuery(id+"F4.boolean.opBoolean","MERGE",FACE,{"derivedFrom":[makeQuery(id+"F1.opExtrude","CAP_FACE",FACE,{"disambiguationData":[OSD([sQuery(id+"F0.wireOp",EDGE,"E0.bottom"),sQuery(id+"F0.wireOp",EDGE,"E0.top"),sQuery(id+"F0.wireOp",EDGE,"E0.left"),sQuery(id+"F0.wireOp",EDGE,"E0.right"),sQuery(id+"F0.wireOp",EDGE,"E4"),sQuery(id+"F0.wireOp",EDGE,"E5")])],"isStart":false}),makeQuery(id+"F4.opExtrude","CAP_FACE",FACE,{"disambiguationData":[OSD([sQuery(id+"F3.wireOp",EDGE,"E6.0"),sQuery(id+"F3.wireOp",EDGE,"E7")])],"isStart":true}),makeQuery(id+"F4.opExtrude","CAP_FACE",FACE,{"disambiguationData":[OSD([sQuery(id+"F3.wireOp",EDGE,"E6.1"),sQuery(id+"F3.wireOp",EDGE,"E8")])],"isStart":true})]}),makeQuery(id+"F9.opExtrude","SWEPT_FACE",FACE,{"disambiguationData":[OSD([sQuery(id+"F8.wireOp",EDGE,"E11.2.0.4")])]})]});
            var Q35;
            Q35=makeQuery(id+"F9.boolean.opBoolean","INTERSECT",EDGE,{"derivedFrom":[makeQuery(id+"F4.boolean.opBoolean","MERGE",FACE,{"derivedFrom":[makeQuery(id+"F1.opExtrude","CAP_FACE",FACE,{"disambiguationData":[OSD([sQuery(id+"F0.wireOp",EDGE,"E0.bottom"),sQuery(id+"F0.wireOp",EDGE,"E0.top"),sQuery(id+"F0.wireOp",EDGE,"E0.left"),sQuery(id+"F0.wireOp",EDGE,"E0.right"),sQuery(id+"F0.wireOp",EDGE,"E4"),sQuery(id+"F0.wireOp",EDGE,"E5")])],"isStart":false}),makeQuery(id+"F4.opExtrude","CAP_FACE",FACE,{"disambiguationData":[OSD([sQuery(id+"F3.wireOp",EDGE,"E6.0"),sQuery(id+"F3.wireOp",EDGE,"E7")])],"isStart":true}),makeQuery(id+"F4.opExtrude","CAP_FACE",FACE,{"disambiguationData":[OSD([sQuery(id+"F3.wireOp",EDGE,"E6.1"),sQuery(id+"F3.wireOp",EDGE,"E8")])],"isStart":true})]}),makeQuery(id+"F9.opExtrude","SWEPT_FACE",FACE,{"disambiguationData":[OSD([sQuery(id+"F8.wireOp",EDGE,"E11.2.0.1")])]})]});
            var Q36;
            Q36=makeQuery(id+"F9.boolean.opBoolean","INTERSECT",EDGE,{"derivedFrom":[makeQuery(id+"F4.boolean.opBoolean","MERGE",FACE,{"derivedFrom":[makeQuery(id+"F1.opExtrude","CAP_FACE",FACE,{"disambiguationData":[OSD([sQuery(id+"F0.wireOp",EDGE,"E0.bottom"),sQuery(id+"F0.wireOp",EDGE,"E0.top"),sQuery(id+"F0.wireOp",EDGE,"E0.left"),sQuery(id+"F0.wireOp",EDGE,"E0.right"),sQuery(id+"F0.wireOp",EDGE,"E4"),sQuery(id+"F0.wireOp",EDGE,"E5")])],"isStart":false}),makeQuery(id+"F4.opExtrude","CAP_FACE",FACE,{"disambiguationData":[OSD([sQuery(id+"F3.wireOp",EDGE,"E6.0"),sQuery(id+"F3.wireOp",EDGE,"E7")])],"isStart":true}),makeQuery(id+"F4.opExtrude","CAP_FACE",FACE,{"disambiguationData":[OSD([sQuery(id+"F3.wireOp",EDGE,"E6.1"),sQuery(id+"F3.wireOp",EDGE,"E8")])],"isStart":true})]}),makeQuery(id+"F9.opExtrude","SWEPT_FACE",FACE,{"disambiguationData":[OSD([sQuery(id+"F8.wireOp",EDGE,"E11.1.0.4")])]})]});
            var Q37;
            Q37=makeQuery(id+"F9.boolean.opBoolean","INTERSECT",EDGE,{"derivedFrom":[makeQuery(id+"F4.boolean.opBoolean","MERGE",FACE,{"derivedFrom":[makeQuery(id+"F1.opExtrude","CAP_FACE",FACE,{"disambiguationData":[OSD([sQuery(id+"F0.wireOp",EDGE,"E0.bottom"),sQuery(id+"F0.wireOp",EDGE,"E0.top"),sQuery(id+"F0.wireOp",EDGE,"E0.left"),sQuery(id+"F0.wireOp",EDGE,"E0.right"),sQuery(id+"F0.wireOp",EDGE,"E4"),sQuery(id+"F0.wireOp",EDGE,"E5")])],"isStart":false}),makeQuery(id+"F4.opExtrude","CAP_FACE",FACE,{"disambiguationData":[OSD([sQuery(id+"F3.wireOp",EDGE,"E6.0"),sQuery(id+"F3.wireOp",EDGE,"E7")])],"isStart":true}),makeQuery(id+"F4.opExtrude","CAP_FACE",FACE,{"disambiguationData":[OSD([sQuery(id+"F3.wireOp",EDGE,"E6.1"),sQuery(id+"F3.wireOp",EDGE,"E8")])],"isStart":true})]}),makeQuery(id+"F9.opExtrude","SWEPT_FACE",FACE,{"disambiguationData":[OSD([sQuery(id+"F8.wireOp",EDGE,"E11.1.0.1")])]})]});
            var Q38;
            Q38=makeQuery(id+"F9.boolean.opBoolean","INTERSECT",EDGE,{"derivedFrom":[makeQuery(id+"F4.boolean.opBoolean","MERGE",FACE,{"derivedFrom":[makeQuery(id+"F1.opExtrude","CAP_FACE",FACE,{"disambiguationData":[OSD([sQuery(id+"F0.wireOp",EDGE,"E0.bottom"),sQuery(id+"F0.wireOp",EDGE,"E0.top"),sQuery(id+"F0.wireOp",EDGE,"E0.left"),sQuery(id+"F0.wireOp",EDGE,"E0.right"),sQuery(id+"F0.wireOp",EDGE,"E4"),sQuery(id+"F0.wireOp",EDGE,"E5")])],"isStart":false}),makeQuery(id+"F4.opExtrude","CAP_FACE",FACE,{"disambiguationData":[OSD([sQuery(id+"F3.wireOp",EDGE,"E6.0"),sQuery(id+"F3.wireOp",EDGE,"E7")])],"isStart":true}),makeQuery(id+"F4.opExtrude","CAP_FACE",FACE,{"disambiguationData":[OSD([sQuery(id+"F3.wireOp",EDGE,"E6.1"),sQuery(id+"F3.wireOp",EDGE,"E8")])],"isStart":true})]}),makeQuery(id+"F9.opExtrude","SWEPT_FACE",FACE,{"disambiguationData":[OSD([sQuery(id+"F8.wireOp",EDGE,"E10.bottom")])]})]});
            var Q39;
            Q39=makeQuery(id+"F9.boolean.opBoolean","INTERSECT",EDGE,{"derivedFrom":[makeQuery(id+"F4.boolean.opBoolean","MERGE",FACE,{"derivedFrom":[makeQuery(id+"F1.opExtrude","CAP_FACE",FACE,{"disambiguationData":[OSD([sQuery(id+"F0.wireOp",EDGE,"E0.bottom"),sQuery(id+"F0.wireOp",EDGE,"E0.top"),sQuery(id+"F0.wireOp",EDGE,"E0.left"),sQuery(id+"F0.wireOp",EDGE,"E0.right"),sQuery(id+"F0.wireOp",EDGE,"E4"),sQuery(id+"F0.wireOp",EDGE,"E5")])],"isStart":false}),makeQuery(id+"F4.opExtrude","CAP_FACE",FACE,{"disambiguationData":[OSD([sQuery(id+"F3.wireOp",EDGE,"E6.0"),sQuery(id+"F3.wireOp",EDGE,"E7")])],"isStart":true}),makeQuery(id+"F4.opExtrude","CAP_FACE",FACE,{"disambiguationData":[OSD([sQuery(id+"F3.wireOp",EDGE,"E6.1"),sQuery(id+"F3.wireOp",EDGE,"E8")])],"isStart":true})]}),makeQuery(id+"F9.opExtrude","SWEPT_FACE",FACE,{"disambiguationData":[OSD([sQuery(id+"F8.wireOp",EDGE,"E10.right")])]})]});
            fillet(context, id + "F10", {"entities" : qUnion([Q0, Q1, Q2, Q3, Q4, Q5, Q6, Q7, Q8, Q9, Q10, Q11, Q12, Q13, Q14, Q15, Q16, Q17, Q18, Q19, Q20, Q21, Q22, Q23, Q24, Q25, Q26, Q27, Q28, Q29, Q30, Q31, Q32, Q33, Q34, Q35, Q36, Q37, Q38, Q39]), "radius" : 0.4 * mm, "tangentPropagation" : true, "allowEdgeOverflow" : false});
        }
        {
            var Q0;
            Q0=makeQuery(id+"F9.opExtrude","CAP_FACE",FACE,{"disambiguationData":[OSD([sQuery(id+"F8.wireOp",EDGE,"E11.9.0.0"),sQuery(id+"F8.wireOp",EDGE,"E11.9.0.1"),sQuery(id+"F8.wireOp",EDGE,"E11.9.0.2"),sQuery(id+"F8.wireOp",EDGE,"E11.9.0.4")])],"isStart":true});
            var Q1;
            Q1=makeQuery(id+"F9.opExtrude","CAP_EDGE",EDGE,{"disambiguationData":[OSD([sQuery(id+"F8.wireOp",EDGE,"E10.left")])],"isStart":true});
            var Q2;
            Q2=makeQuery(id+"F9.opExtrude","CAP_EDGE",EDGE,{"disambiguationData":[OSD([sQuery(id+"F8.wireOp",EDGE,"E11.1.0.0")])],"isStart":true});
            var Q3;
            Q3=makeQuery(id+"F9.opExtrude","CAP_EDGE",EDGE,{"disambiguationData":[OSD([sQuery(id+"F8.wireOp",EDGE,"E11.2.0.0")])],"isStart":true});
            var Q4;
            Q4=makeQuery(id+"F9.opExtrude","CAP_EDGE",EDGE,{"disambiguationData":[OSD([sQuery(id+"F8.wireOp",EDGE,"E11.3.0.0")])],"isStart":true});
            var Q5;
            Q5=makeQuery(id+"F9.opExtrude","CAP_EDGE",EDGE,{"disambiguationData":[OSD([sQuery(id+"F8.wireOp",EDGE,"E11.4.0.0")])],"isStart":true});
            var Q6;
            Q6=makeQuery(id+"F9.opExtrude","CAP_EDGE",EDGE,{"disambiguationData":[OSD([sQuery(id+"F8.wireOp",EDGE,"E11.5.0.0")])],"isStart":true});
            var Q7;
            Q7=makeQuery(id+"F9.opExtrude","CAP_EDGE",EDGE,{"disambiguationData":[OSD([sQuery(id+"F8.wireOp",EDGE,"E11.6.0.0")])],"isStart":true});
            var Q8;
            Q8=makeQuery(id+"F9.opExtrude","CAP_EDGE",EDGE,{"disambiguationData":[OSD([sQuery(id+"F8.wireOp",EDGE,"E11.7.0.0")])],"isStart":true});
            var Q9;
            Q9=makeQuery(id+"F9.opExtrude","CAP_EDGE",EDGE,{"disambiguationData":[OSD([sQuery(id+"F8.wireOp",EDGE,"E11.8.0.0")])],"isStart":true});
            var Q10;
            Q10=makeQuery(id+"F9.opExtrude","CAP_EDGE",EDGE,{"disambiguationData":[OSD([sQuery(id+"F8.wireOp",EDGE,"E11.8.0.2")])],"isStart":true});
            var Q11;
            Q11=makeQuery(id+"F9.opExtrude","CAP_EDGE",EDGE,{"disambiguationData":[OSD([sQuery(id+"F8.wireOp",EDGE,"E11.7.0.2")])],"isStart":true});
            var Q12;
            Q12=makeQuery(id+"F9.opExtrude","CAP_EDGE",EDGE,{"disambiguationData":[OSD([sQuery(id+"F8.wireOp",EDGE,"E11.6.0.2")])],"isStart":true});
            var Q13;
            Q13=makeQuery(id+"F9.opExtrude","CAP_EDGE",EDGE,{"disambiguationData":[OSD([sQuery(id+"F8.wireOp",EDGE,"E11.5.0.2")])],"isStart":true});
            var Q14;
            Q14=makeQuery(id+"F9.opExtrude","CAP_EDGE",EDGE,{"disambiguationData":[OSD([sQuery(id+"F8.wireOp",EDGE,"E11.4.0.2")])],"isStart":true});
            var Q15;
            Q15=makeQuery(id+"F9.opExtrude","CAP_EDGE",EDGE,{"disambiguationData":[OSD([sQuery(id+"F8.wireOp",EDGE,"E11.3.0.2")])],"isStart":true});
            var Q16;
            Q16=makeQuery(id+"F9.opExtrude","CAP_EDGE",EDGE,{"disambiguationData":[OSD([sQuery(id+"F8.wireOp",EDGE,"E11.2.0.2")])],"isStart":true});
            var Q17;
            Q17=makeQuery(id+"F9.opExtrude","CAP_EDGE",EDGE,{"disambiguationData":[OSD([sQuery(id+"F8.wireOp",EDGE,"E11.1.0.2")])],"isStart":true});
            var Q18;
            Q18=makeQuery(id+"F9.opExtrude","CAP_EDGE",EDGE,{"disambiguationData":[OSD([sQuery(id+"F8.wireOp",EDGE,"E10.top")])],"isStart":true});
            var Q19;
            Q19=makeQuery(id+"F9.opExtrude","CAP_EDGE",EDGE,{"disambiguationData":[OSD([sQuery(id+"F8.wireOp",EDGE,"E11.9.0.4")])],"isStart":false});
            var Q20;
            Q20=makeQuery(id+"F9.opExtrude","CAP_EDGE",EDGE,{"disambiguationData":[OSD([sQuery(id+"F8.wireOp",EDGE,"E11.9.0.1")])],"isStart":false});
            var Q21;
            Q21=makeQuery(id+"F9.opExtrude","CAP_EDGE",EDGE,{"disambiguationData":[OSD([sQuery(id+"F8.wireOp",EDGE,"E11.8.0.4")])],"isStart":false});
            var Q22;
            Q22=makeQuery(id+"F9.opExtrude","CAP_EDGE",EDGE,{"disambiguationData":[OSD([sQuery(id+"F8.wireOp",EDGE,"E11.8.0.1")])],"isStart":false});
            var Q23;
            Q23=makeQuery(id+"F9.opExtrude","CAP_EDGE",EDGE,{"disambiguationData":[OSD([sQuery(id+"F8.wireOp",EDGE,"E11.7.0.4")])],"isStart":false});
            var Q24;
            Q24=makeQuery(id+"F9.opExtrude","CAP_EDGE",EDGE,{"disambiguationData":[OSD([sQuery(id+"F8.wireOp",EDGE,"E11.7.0.1")])],"isStart":false});
            var Q25;
            Q25=makeQuery(id+"F9.opExtrude","CAP_EDGE",EDGE,{"disambiguationData":[OSD([sQuery(id+"F8.wireOp",EDGE,"E11.6.0.4")])],"isStart":false});
            var Q26;
            Q26=makeQuery(id+"F9.opExtrude","CAP_EDGE",EDGE,{"disambiguationData":[OSD([sQuery(id+"F8.wireOp",EDGE,"E11.6.0.1")])],"isStart":false});
            var Q27;
            Q27=makeQuery(id+"F9.opExtrude","CAP_EDGE",EDGE,{"disambiguationData":[OSD([sQuery(id+"F8.wireOp",EDGE,"E11.5.0.4")])],"isStart":false});
            var Q28;
            Q28=makeQuery(id+"F9.opExtrude","CAP_EDGE",EDGE,{"disambiguationData":[OSD([sQuery(id+"F8.wireOp",EDGE,"E11.5.0.1")])],"isStart":false});
            var Q29;
            Q29=makeQuery(id+"F9.opExtrude","CAP_EDGE",EDGE,{"disambiguationData":[OSD([sQuery(id+"F8.wireOp",EDGE,"E11.4.0.4")])],"isStart":false});
            var Q30;
            Q30=makeQuery(id+"F9.opExtrude","CAP_EDGE",EDGE,{"disambiguationData":[OSD([sQuery(id+"F8.wireOp",EDGE,"E11.4.0.1")])],"isStart":false});
            var Q31;
            Q31=makeQuery(id+"F9.opExtrude","CAP_EDGE",EDGE,{"disambiguationData":[OSD([sQuery(id+"F8.wireOp",EDGE,"E11.3.0.4")])],"isStart":false});
            var Q32;
            Q32=makeQuery(id+"F9.opExtrude","CAP_EDGE",EDGE,{"disambiguationData":[OSD([sQuery(id+"F8.wireOp",EDGE,"E11.3.0.1")])],"isStart":false});
            var Q33;
            Q33=makeQuery(id+"F9.opExtrude","CAP_EDGE",EDGE,{"disambiguationData":[OSD([sQuery(id+"F8.wireOp",EDGE,"E11.2.0.4")])],"isStart":false});
            var Q34;
            Q34=makeQuery(id+"F9.opExtrude","CAP_EDGE",EDGE,{"disambiguationData":[OSD([sQuery(id+"F8.wireOp",EDGE,"E11.2.0.1")])],"isStart":false});
            var Q35;
            Q35=makeQuery(id+"F9.opExtrude","CAP_EDGE",EDGE,{"disambiguationData":[OSD([sQuery(id+"F8.wireOp",EDGE,"E11.1.0.4")])],"isStart":false});
            var Q36;
            Q36=makeQuery(id+"F9.opExtrude","CAP_EDGE",EDGE,{"disambiguationData":[OSD([sQuery(id+"F8.wireOp",EDGE,"E11.1.0.1")])],"isStart":false});
            var Q37;
            Q37=makeQuery(id+"F9.opExtrude","CAP_EDGE",EDGE,{"disambiguationData":[OSD([sQuery(id+"F8.wireOp",EDGE,"E10.bottom")])],"isStart":false});
            var Q38;
            Q38=makeQuery(id+"F9.opExtrude","CAP_EDGE",EDGE,{"disambiguationData":[OSD([sQuery(id+"F8.wireOp",EDGE,"E10.right")])],"isStart":false});
            chamfer(context, id + "F11", {"entities" : qUnion([Q0, Q1, Q2, Q3, Q4, Q5, Q6, Q7, Q8, Q9, Q10, Q11, Q12, Q13, Q14, Q15, Q16, Q17, Q18, Q19, Q20, Q21, Q22, Q23, Q24, Q25, Q26, Q27, Q28, Q29, Q30, Q31, Q32, Q33, Q34, Q35, Q36, Q37, Q38]), "chamferType" : ChamferType.OFFSET_ANGLE, "width" : 0.5 * mm, "oppositeDirection" : false, "angle" : 60 * degree, "tangentPropagation" : true});
        }
        {
            var Q0;
            Q0=makeQuery(id+"F9.opExtrude","CAP_EDGE",EDGE,{"disambiguationData":[OSD([sQuery(id+"F8.wireOp",EDGE,"E10.top")])],"isStart":false});
            var Q1;
            Q1=makeQuery(id+"F9.opExtrude","CAP_EDGE",EDGE,{"disambiguationData":[OSD([sQuery(id+"F8.wireOp",EDGE,"E10.left")])],"isStart":false});
            var Q2;
            Q2=makeQuery(id+"F9.opExtrude","CAP_EDGE",EDGE,{"disambiguationData":[OSD([sQuery(id+"F8.wireOp",EDGE,"E11.1.0.2")])],"isStart":false});
            var Q3;
            Q3=makeQuery(id+"F9.opExtrude","CAP_EDGE",EDGE,{"disambiguationData":[OSD([sQuery(id+"F8.wireOp",EDGE,"E11.1.0.0")])],"isStart":false});
            var Q4;
            Q4=makeQuery(id+"F9.opExtrude","CAP_EDGE",EDGE,{"disambiguationData":[OSD([sQuery(id+"F8.wireOp",EDGE,"E11.2.0.2")])],"isStart":false});
            var Q5;
            Q5=makeQuery(id+"F9.opExtrude","CAP_EDGE",EDGE,{"disambiguationData":[OSD([sQuery(id+"F8.wireOp",EDGE,"E11.2.0.0")])],"isStart":false});
            var Q6;
            Q6=makeQuery(id+"F9.opExtrude","CAP_EDGE",EDGE,{"disambiguationData":[OSD([sQuery(id+"F8.wireOp",EDGE,"E11.3.0.2")])],"isStart":false});
            var Q7;
            Q7=makeQuery(id+"F9.opExtrude","CAP_EDGE",EDGE,{"disambiguationData":[OSD([sQuery(id+"F8.wireOp",EDGE,"E11.3.0.0")])],"isStart":false});
            var Q8;
            Q8=makeQuery(id+"F9.opExtrude","CAP_EDGE",EDGE,{"disambiguationData":[OSD([sQuery(id+"F8.wireOp",EDGE,"E11.4.0.2")])],"isStart":false});
            var Q9;
            Q9=makeQuery(id+"F9.opExtrude","CAP_EDGE",EDGE,{"disambiguationData":[OSD([sQuery(id+"F8.wireOp",EDGE,"E11.4.0.0")])],"isStart":false});
            var Q10;
            Q10=makeQuery(id+"F9.opExtrude","CAP_EDGE",EDGE,{"disambiguationData":[OSD([sQuery(id+"F8.wireOp",EDGE,"E11.5.0.2")])],"isStart":false});
            var Q11;
            Q11=makeQuery(id+"F9.opExtrude","CAP_EDGE",EDGE,{"disambiguationData":[OSD([sQuery(id+"F8.wireOp",EDGE,"E11.5.0.0")])],"isStart":false});
            var Q12;
            Q12=makeQuery(id+"F9.opExtrude","CAP_EDGE",EDGE,{"disambiguationData":[OSD([sQuery(id+"F8.wireOp",EDGE,"E11.6.0.2")])],"isStart":false});
            var Q13;
            Q13=makeQuery(id+"F9.opExtrude","CAP_EDGE",EDGE,{"disambiguationData":[OSD([sQuery(id+"F8.wireOp",EDGE,"E11.6.0.0")])],"isStart":false});
            var Q14;
            Q14=makeQuery(id+"F9.opExtrude","CAP_EDGE",EDGE,{"disambiguationData":[OSD([sQuery(id+"F8.wireOp",EDGE,"E11.7.0.2")])],"isStart":false});
            var Q15;
            Q15=makeQuery(id+"F9.opExtrude","CAP_EDGE",EDGE,{"disambiguationData":[OSD([sQuery(id+"F8.wireOp",EDGE,"E11.7.0.0")])],"isStart":false});
            var Q16;
            Q16=makeQuery(id+"F9.opExtrude","CAP_EDGE",EDGE,{"disambiguationData":[OSD([sQuery(id+"F8.wireOp",EDGE,"E11.8.0.2")])],"isStart":false});
            var Q17;
            Q17=makeQuery(id+"F9.opExtrude","CAP_EDGE",EDGE,{"disambiguationData":[OSD([sQuery(id+"F8.wireOp",EDGE,"E11.8.0.0")])],"isStart":false});
            var Q18;
            Q18=makeQuery(id+"F9.opExtrude","CAP_EDGE",EDGE,{"disambiguationData":[OSD([sQuery(id+"F8.wireOp",EDGE,"E11.9.0.2")])],"isStart":false});
            var Q19;
            Q19=makeQuery(id+"F9.opExtrude","CAP_EDGE",EDGE,{"disambiguationData":[OSD([sQuery(id+"F8.wireOp",EDGE,"E11.9.0.0")])],"isStart":false});
            var Q20;
            Q20=makeQuery(id+"F9.opExtrude","CAP_EDGE",EDGE,{"disambiguationData":[OSD([sQuery(id+"F8.wireOp",EDGE,"E11.8.0.4")])],"isStart":true});
            var Q21;
            Q21=makeQuery(id+"F9.opExtrude","CAP_EDGE",EDGE,{"disambiguationData":[OSD([sQuery(id+"F8.wireOp",EDGE,"E11.8.0.1")])],"isStart":true});
            var Q22;
            Q22=makeQuery(id+"F9.opExtrude","CAP_EDGE",EDGE,{"disambiguationData":[OSD([sQuery(id+"F8.wireOp",EDGE,"E11.7.0.4")])],"isStart":true});
            var Q23;
            Q23=makeQuery(id+"F9.opExtrude","CAP_EDGE",EDGE,{"disambiguationData":[OSD([sQuery(id+"F8.wireOp",EDGE,"E11.7.0.1")])],"isStart":true});
            var Q24;
            Q24=makeQuery(id+"F9.opExtrude","CAP_EDGE",EDGE,{"disambiguationData":[OSD([sQuery(id+"F8.wireOp",EDGE,"E11.6.0.4")])],"isStart":true});
            var Q25;
            Q25=makeQuery(id+"F9.opExtrude","CAP_EDGE",EDGE,{"disambiguationData":[OSD([sQuery(id+"F8.wireOp",EDGE,"E11.6.0.1")])],"isStart":true});
            var Q26;
            Q26=makeQuery(id+"F9.opExtrude","CAP_EDGE",EDGE,{"disambiguationData":[OSD([sQuery(id+"F8.wireOp",EDGE,"E11.5.0.4")])],"isStart":true});
            var Q27;
            Q27=makeQuery(id+"F9.opExtrude","CAP_EDGE",EDGE,{"disambiguationData":[OSD([sQuery(id+"F8.wireOp",EDGE,"E11.5.0.1")])],"isStart":true});
            var Q28;
            Q28=makeQuery(id+"F9.opExtrude","CAP_EDGE",EDGE,{"disambiguationData":[OSD([sQuery(id+"F8.wireOp",EDGE,"E11.4.0.4")])],"isStart":true});
            var Q29;
            Q29=makeQuery(id+"F9.opExtrude","CAP_EDGE",EDGE,{"disambiguationData":[OSD([sQuery(id+"F8.wireOp",EDGE,"E11.4.0.1")])],"isStart":true});
            var Q30;
            Q30=makeQuery(id+"F9.opExtrude","CAP_EDGE",EDGE,{"disambiguationData":[OSD([sQuery(id+"F8.wireOp",EDGE,"E11.3.0.4")])],"isStart":true});
            var Q31;
            Q31=makeQuery(id+"F9.opExtrude","CAP_EDGE",EDGE,{"disambiguationData":[OSD([sQuery(id+"F8.wireOp",EDGE,"E11.3.0.1")])],"isStart":true});
            var Q32;
            Q32=makeQuery(id+"F9.opExtrude","CAP_EDGE",EDGE,{"disambiguationData":[OSD([sQuery(id+"F8.wireOp",EDGE,"E11.2.0.4")])],"isStart":true});
            var Q33;
            Q33=makeQuery(id+"F9.opExtrude","CAP_EDGE",EDGE,{"disambiguationData":[OSD([sQuery(id+"F8.wireOp",EDGE,"E11.2.0.1")])],"isStart":true});
            var Q34;
            Q34=makeQuery(id+"F9.opExtrude","CAP_EDGE",EDGE,{"disambiguationData":[OSD([sQuery(id+"F8.wireOp",EDGE,"E11.1.0.4")])],"isStart":true});
            var Q35;
            Q35=makeQuery(id+"F9.opExtrude","CAP_EDGE",EDGE,{"disambiguationData":[OSD([sQuery(id+"F8.wireOp",EDGE,"E11.1.0.1")])],"isStart":true});
            var Q36;
            Q36=makeQuery(id+"F9.opExtrude","CAP_EDGE",EDGE,{"disambiguationData":[OSD([sQuery(id+"F8.wireOp",EDGE,"E10.bottom")])],"isStart":true});
            var Q37;
            Q37=makeQuery(id+"F9.opExtrude","CAP_EDGE",EDGE,{"disambiguationData":[OSD([sQuery(id+"F8.wireOp",EDGE,"E10.right")])],"isStart":true});
            chamfer(context, id + "F12", {"entities" : qUnion([Q0, Q1, Q2, Q3, Q4, Q5, Q6, Q7, Q8, Q9, Q10, Q11, Q12, Q13, Q14, Q15, Q16, Q17, Q18, Q19, Q20, Q21, Q22, Q23, Q24, Q25, Q26, Q27, Q28, Q29, Q30, Q31, Q32, Q33, Q34, Q35, Q36, Q37]), "chamferType" : ChamferType.OFFSET_ANGLE, "width" : 0.5 * mm, "oppositeDirection" : true, "angle" : 60 * degree, "tangentPropagation" : true});
        }
        {
            var Q0;
            {var subQ0=makeQuery(id+"F4.boolean.opBoolean","MERGE",FACE,{"derivedFrom":[makeQuery(id+"F1.opExtrude","CAP_FACE",FACE,{"disambiguationData":[OSD([sQuery(id+"F0.wireOp",EDGE,"E0.bottom"),sQuery(id+"F0.wireOp",EDGE,"E0.top"),sQuery(id+"F0.wireOp",EDGE,"E0.left"),sQuery(id+"F0.wireOp",EDGE,"E0.right"),sQuery(id+"F0.wireOp",EDGE,"E4"),sQuery(id+"F0.wireOp",EDGE,"E5")])],"isStart":false}),makeQuery(id+"F4.opExtrude","CAP_FACE",FACE,{"disambiguationData":[OSD([sQuery(id+"F3.wireOp",EDGE,"E6.0"),sQuery(id+"F3.wireOp",EDGE,"E7")])],"isStart":true}),makeQuery(id+"F4.opExtrude","CAP_FACE",FACE,{"disambiguationData":[OSD([sQuery(id+"F3.wireOp",EDGE,"E6.1"),sQuery(id+"F3.wireOp",EDGE,"E8")])],"isStart":true})]});Q0=makeQuery(id+"F10.opFillet","BLEND_EDGE",EDGE,{"blendedFrom":[makeQuery(id+"F9.boolean.opBoolean","INTERSECT",EDGE,{"derivedFrom":[subQ0,makeQuery(id+"F9.opExtrude","SWEPT_FACE",FACE,{"disambiguationData":[OSD([sQuery(id+"F8.wireOp",EDGE,"E11.9.0.0")])]})]}),makeQuery(id+"F9.boolean.opBoolean","INTERSECT",EDGE,{"derivedFrom":[subQ0,makeQuery(id+"F9.opExtrude","SWEPT_FACE",FACE,{"disambiguationData":[OSD([sQuery(id+"F8.wireOp",EDGE,"E11.9.0.4")])]})]})],"blendedInto":[]});}
            var Q1;
            {var subQ0=makeQuery(id+"F4.boolean.opBoolean","MERGE",FACE,{"derivedFrom":[makeQuery(id+"F1.opExtrude","CAP_FACE",FACE,{"disambiguationData":[OSD([sQuery(id+"F0.wireOp",EDGE,"E0.bottom"),sQuery(id+"F0.wireOp",EDGE,"E0.top"),sQuery(id+"F0.wireOp",EDGE,"E0.left"),sQuery(id+"F0.wireOp",EDGE,"E0.right"),sQuery(id+"F0.wireOp",EDGE,"E4"),sQuery(id+"F0.wireOp",EDGE,"E5")])],"isStart":false}),makeQuery(id+"F4.opExtrude","CAP_FACE",FACE,{"disambiguationData":[OSD([sQuery(id+"F3.wireOp",EDGE,"E6.0"),sQuery(id+"F3.wireOp",EDGE,"E7")])],"isStart":true}),makeQuery(id+"F4.opExtrude","CAP_FACE",FACE,{"disambiguationData":[OSD([sQuery(id+"F3.wireOp",EDGE,"E6.1"),sQuery(id+"F3.wireOp",EDGE,"E8")])],"isStart":true})]});Q1=makeQuery(id+"F10.opFillet","BLEND_EDGE",EDGE,{"blendedFrom":[makeQuery(id+"F9.boolean.opBoolean","INTERSECT",EDGE,{"derivedFrom":[subQ0,makeQuery(id+"F9.opExtrude","SWEPT_FACE",FACE,{"disambiguationData":[OSD([sQuery(id+"F8.wireOp",EDGE,"E11.9.0.0")])]})]}),makeQuery(id+"F9.boolean.opBoolean","INTERSECT",EDGE,{"derivedFrom":[subQ0,makeQuery(id+"F9.opExtrude","SWEPT_FACE",FACE,{"disambiguationData":[OSD([sQuery(id+"F8.wireOp",EDGE,"E11.9.0.2")])]})]})],"blendedInto":[]});}
            var Q2;
            {var subQ0=makeQuery(id+"F4.boolean.opBoolean","MERGE",FACE,{"derivedFrom":[makeQuery(id+"F1.opExtrude","CAP_FACE",FACE,{"disambiguationData":[OSD([sQuery(id+"F0.wireOp",EDGE,"E0.bottom"),sQuery(id+"F0.wireOp",EDGE,"E0.top"),sQuery(id+"F0.wireOp",EDGE,"E0.left"),sQuery(id+"F0.wireOp",EDGE,"E0.right"),sQuery(id+"F0.wireOp",EDGE,"E4"),sQuery(id+"F0.wireOp",EDGE,"E5")])],"isStart":false}),makeQuery(id+"F4.opExtrude","CAP_FACE",FACE,{"disambiguationData":[OSD([sQuery(id+"F3.wireOp",EDGE,"E6.0"),sQuery(id+"F3.wireOp",EDGE,"E7")])],"isStart":true}),makeQuery(id+"F4.opExtrude","CAP_FACE",FACE,{"disambiguationData":[OSD([sQuery(id+"F3.wireOp",EDGE,"E6.1"),sQuery(id+"F3.wireOp",EDGE,"E8")])],"isStart":true})]});Q2=makeQuery(id+"F10.opFillet","BLEND_EDGE",EDGE,{"blendedFrom":[makeQuery(id+"F9.boolean.opBoolean","INTERSECT",EDGE,{"derivedFrom":[subQ0,makeQuery(id+"F9.opExtrude","SWEPT_FACE",FACE,{"disambiguationData":[OSD([sQuery(id+"F8.wireOp",EDGE,"E11.9.0.1")])]})]}),makeQuery(id+"F9.boolean.opBoolean","INTERSECT",EDGE,{"derivedFrom":[subQ0,makeQuery(id+"F9.opExtrude","SWEPT_FACE",FACE,{"disambiguationData":[OSD([sQuery(id+"F8.wireOp",EDGE,"E11.9.0.2")])]})]})],"blendedInto":[]});}
            var Q3;
            {var subQ0=makeQuery(id+"F4.boolean.opBoolean","MERGE",FACE,{"derivedFrom":[makeQuery(id+"F1.opExtrude","CAP_FACE",FACE,{"disambiguationData":[OSD([sQuery(id+"F0.wireOp",EDGE,"E0.bottom"),sQuery(id+"F0.wireOp",EDGE,"E0.top"),sQuery(id+"F0.wireOp",EDGE,"E0.left"),sQuery(id+"F0.wireOp",EDGE,"E0.right"),sQuery(id+"F0.wireOp",EDGE,"E4"),sQuery(id+"F0.wireOp",EDGE,"E5")])],"isStart":false}),makeQuery(id+"F4.opExtrude","CAP_FACE",FACE,{"disambiguationData":[OSD([sQuery(id+"F3.wireOp",EDGE,"E6.0"),sQuery(id+"F3.wireOp",EDGE,"E7")])],"isStart":true}),makeQuery(id+"F4.opExtrude","CAP_FACE",FACE,{"disambiguationData":[OSD([sQuery(id+"F3.wireOp",EDGE,"E6.1"),sQuery(id+"F3.wireOp",EDGE,"E8")])],"isStart":true})]});Q3=makeQuery(id+"F10.opFillet","BLEND_EDGE",EDGE,{"blendedFrom":[makeQuery(id+"F9.boolean.opBoolean","INTERSECT",EDGE,{"derivedFrom":[subQ0,makeQuery(id+"F9.opExtrude","SWEPT_FACE",FACE,{"disambiguationData":[OSD([sQuery(id+"F8.wireOp",EDGE,"E11.9.0.1")])]})]}),makeQuery(id+"F9.boolean.opBoolean","INTERSECT",EDGE,{"derivedFrom":[subQ0,makeQuery(id+"F9.opExtrude","SWEPT_FACE",FACE,{"disambiguationData":[OSD([sQuery(id+"F8.wireOp",EDGE,"E11.9.0.4")])]})]})],"blendedInto":[]});}
            var Q4;
            {var subQ0=makeQuery(id+"F4.boolean.opBoolean","MERGE",FACE,{"derivedFrom":[makeQuery(id+"F1.opExtrude","CAP_FACE",FACE,{"disambiguationData":[OSD([sQuery(id+"F0.wireOp",EDGE,"E0.bottom"),sQuery(id+"F0.wireOp",EDGE,"E0.top"),sQuery(id+"F0.wireOp",EDGE,"E0.left"),sQuery(id+"F0.wireOp",EDGE,"E0.right"),sQuery(id+"F0.wireOp",EDGE,"E4"),sQuery(id+"F0.wireOp",EDGE,"E5")])],"isStart":false}),makeQuery(id+"F4.opExtrude","CAP_FACE",FACE,{"disambiguationData":[OSD([sQuery(id+"F3.wireOp",EDGE,"E6.0"),sQuery(id+"F3.wireOp",EDGE,"E7")])],"isStart":true}),makeQuery(id+"F4.opExtrude","CAP_FACE",FACE,{"disambiguationData":[OSD([sQuery(id+"F3.wireOp",EDGE,"E6.1"),sQuery(id+"F3.wireOp",EDGE,"E8")])],"isStart":true})]});Q4=makeQuery(id+"F10.opFillet","BLEND_EDGE",EDGE,{"blendedFrom":[makeQuery(id+"F9.boolean.opBoolean","INTERSECT",EDGE,{"derivedFrom":[subQ0,makeQuery(id+"F9.opExtrude","SWEPT_FACE",FACE,{"disambiguationData":[OSD([sQuery(id+"F8.wireOp",EDGE,"E11.8.0.0")])]})]}),makeQuery(id+"F9.boolean.opBoolean","INTERSECT",EDGE,{"derivedFrom":[subQ0,makeQuery(id+"F9.opExtrude","SWEPT_FACE",FACE,{"disambiguationData":[OSD([sQuery(id+"F8.wireOp",EDGE,"E11.8.0.4")])]})]})],"blendedInto":[]});}
            var Q5;
            {var subQ0=makeQuery(id+"F4.boolean.opBoolean","MERGE",FACE,{"derivedFrom":[makeQuery(id+"F1.opExtrude","CAP_FACE",FACE,{"disambiguationData":[OSD([sQuery(id+"F0.wireOp",EDGE,"E0.bottom"),sQuery(id+"F0.wireOp",EDGE,"E0.top"),sQuery(id+"F0.wireOp",EDGE,"E0.left"),sQuery(id+"F0.wireOp",EDGE,"E0.right"),sQuery(id+"F0.wireOp",EDGE,"E4"),sQuery(id+"F0.wireOp",EDGE,"E5")])],"isStart":false}),makeQuery(id+"F4.opExtrude","CAP_FACE",FACE,{"disambiguationData":[OSD([sQuery(id+"F3.wireOp",EDGE,"E6.0"),sQuery(id+"F3.wireOp",EDGE,"E7")])],"isStart":true}),makeQuery(id+"F4.opExtrude","CAP_FACE",FACE,{"disambiguationData":[OSD([sQuery(id+"F3.wireOp",EDGE,"E6.1"),sQuery(id+"F3.wireOp",EDGE,"E8")])],"isStart":true})]});Q5=makeQuery(id+"F10.opFillet","BLEND_EDGE",EDGE,{"blendedFrom":[makeQuery(id+"F9.boolean.opBoolean","INTERSECT",EDGE,{"derivedFrom":[subQ0,makeQuery(id+"F9.opExtrude","SWEPT_FACE",FACE,{"disambiguationData":[OSD([sQuery(id+"F8.wireOp",EDGE,"E11.8.0.1")])]})]}),makeQuery(id+"F9.boolean.opBoolean","INTERSECT",EDGE,{"derivedFrom":[subQ0,makeQuery(id+"F9.opExtrude","SWEPT_FACE",FACE,{"disambiguationData":[OSD([sQuery(id+"F8.wireOp",EDGE,"E11.8.0.4")])]})]})],"blendedInto":[]});}
            var Q6;
            {var subQ0=makeQuery(id+"F4.boolean.opBoolean","MERGE",FACE,{"derivedFrom":[makeQuery(id+"F1.opExtrude","CAP_FACE",FACE,{"disambiguationData":[OSD([sQuery(id+"F0.wireOp",EDGE,"E0.bottom"),sQuery(id+"F0.wireOp",EDGE,"E0.top"),sQuery(id+"F0.wireOp",EDGE,"E0.left"),sQuery(id+"F0.wireOp",EDGE,"E0.right"),sQuery(id+"F0.wireOp",EDGE,"E4"),sQuery(id+"F0.wireOp",EDGE,"E5")])],"isStart":false}),makeQuery(id+"F4.opExtrude","CAP_FACE",FACE,{"disambiguationData":[OSD([sQuery(id+"F3.wireOp",EDGE,"E6.0"),sQuery(id+"F3.wireOp",EDGE,"E7")])],"isStart":true}),makeQuery(id+"F4.opExtrude","CAP_FACE",FACE,{"disambiguationData":[OSD([sQuery(id+"F3.wireOp",EDGE,"E6.1"),sQuery(id+"F3.wireOp",EDGE,"E8")])],"isStart":true})]});Q6=makeQuery(id+"F10.opFillet","BLEND_EDGE",EDGE,{"blendedFrom":[makeQuery(id+"F9.boolean.opBoolean","INTERSECT",EDGE,{"derivedFrom":[subQ0,makeQuery(id+"F9.opExtrude","SWEPT_FACE",FACE,{"disambiguationData":[OSD([sQuery(id+"F8.wireOp",EDGE,"E11.8.0.1")])]})]}),makeQuery(id+"F9.boolean.opBoolean","INTERSECT",EDGE,{"derivedFrom":[subQ0,makeQuery(id+"F9.opExtrude","SWEPT_FACE",FACE,{"disambiguationData":[OSD([sQuery(id+"F8.wireOp",EDGE,"E11.8.0.2")])]})]})],"blendedInto":[]});}
            var Q7;
            {var subQ0=makeQuery(id+"F4.boolean.opBoolean","MERGE",FACE,{"derivedFrom":[makeQuery(id+"F1.opExtrude","CAP_FACE",FACE,{"disambiguationData":[OSD([sQuery(id+"F0.wireOp",EDGE,"E0.bottom"),sQuery(id+"F0.wireOp",EDGE,"E0.top"),sQuery(id+"F0.wireOp",EDGE,"E0.left"),sQuery(id+"F0.wireOp",EDGE,"E0.right"),sQuery(id+"F0.wireOp",EDGE,"E4"),sQuery(id+"F0.wireOp",EDGE,"E5")])],"isStart":false}),makeQuery(id+"F4.opExtrude","CAP_FACE",FACE,{"disambiguationData":[OSD([sQuery(id+"F3.wireOp",EDGE,"E6.0"),sQuery(id+"F3.wireOp",EDGE,"E7")])],"isStart":true}),makeQuery(id+"F4.opExtrude","CAP_FACE",FACE,{"disambiguationData":[OSD([sQuery(id+"F3.wireOp",EDGE,"E6.1"),sQuery(id+"F3.wireOp",EDGE,"E8")])],"isStart":true})]});Q7=makeQuery(id+"F10.opFillet","BLEND_EDGE",EDGE,{"blendedFrom":[makeQuery(id+"F9.boolean.opBoolean","INTERSECT",EDGE,{"derivedFrom":[subQ0,makeQuery(id+"F9.opExtrude","SWEPT_FACE",FACE,{"disambiguationData":[OSD([sQuery(id+"F8.wireOp",EDGE,"E11.8.0.0")])]})]}),makeQuery(id+"F9.boolean.opBoolean","INTERSECT",EDGE,{"derivedFrom":[subQ0,makeQuery(id+"F9.opExtrude","SWEPT_FACE",FACE,{"disambiguationData":[OSD([sQuery(id+"F8.wireOp",EDGE,"E11.8.0.2")])]})]})],"blendedInto":[]});}
            var Q8;
            {var subQ0=makeQuery(id+"F4.boolean.opBoolean","MERGE",FACE,{"derivedFrom":[makeQuery(id+"F1.opExtrude","CAP_FACE",FACE,{"disambiguationData":[OSD([sQuery(id+"F0.wireOp",EDGE,"E0.bottom"),sQuery(id+"F0.wireOp",EDGE,"E0.top"),sQuery(id+"F0.wireOp",EDGE,"E0.left"),sQuery(id+"F0.wireOp",EDGE,"E0.right"),sQuery(id+"F0.wireOp",EDGE,"E4"),sQuery(id+"F0.wireOp",EDGE,"E5")])],"isStart":false}),makeQuery(id+"F4.opExtrude","CAP_FACE",FACE,{"disambiguationData":[OSD([sQuery(id+"F3.wireOp",EDGE,"E6.0"),sQuery(id+"F3.wireOp",EDGE,"E7")])],"isStart":true}),makeQuery(id+"F4.opExtrude","CAP_FACE",FACE,{"disambiguationData":[OSD([sQuery(id+"F3.wireOp",EDGE,"E6.1"),sQuery(id+"F3.wireOp",EDGE,"E8")])],"isStart":true})]});Q8=makeQuery(id+"F10.opFillet","BLEND_EDGE",EDGE,{"blendedFrom":[makeQuery(id+"F9.boolean.opBoolean","INTERSECT",EDGE,{"derivedFrom":[subQ0,makeQuery(id+"F9.opExtrude","SWEPT_FACE",FACE,{"disambiguationData":[OSD([sQuery(id+"F8.wireOp",EDGE,"E11.7.0.0")])]})]}),makeQuery(id+"F9.boolean.opBoolean","INTERSECT",EDGE,{"derivedFrom":[subQ0,makeQuery(id+"F9.opExtrude","SWEPT_FACE",FACE,{"disambiguationData":[OSD([sQuery(id+"F8.wireOp",EDGE,"E11.7.0.2")])]})]})],"blendedInto":[]});}
            var Q9;
            {var subQ0=makeQuery(id+"F4.boolean.opBoolean","MERGE",FACE,{"derivedFrom":[makeQuery(id+"F1.opExtrude","CAP_FACE",FACE,{"disambiguationData":[OSD([sQuery(id+"F0.wireOp",EDGE,"E0.bottom"),sQuery(id+"F0.wireOp",EDGE,"E0.top"),sQuery(id+"F0.wireOp",EDGE,"E0.left"),sQuery(id+"F0.wireOp",EDGE,"E0.right"),sQuery(id+"F0.wireOp",EDGE,"E4"),sQuery(id+"F0.wireOp",EDGE,"E5")])],"isStart":false}),makeQuery(id+"F4.opExtrude","CAP_FACE",FACE,{"disambiguationData":[OSD([sQuery(id+"F3.wireOp",EDGE,"E6.0"),sQuery(id+"F3.wireOp",EDGE,"E7")])],"isStart":true}),makeQuery(id+"F4.opExtrude","CAP_FACE",FACE,{"disambiguationData":[OSD([sQuery(id+"F3.wireOp",EDGE,"E6.1"),sQuery(id+"F3.wireOp",EDGE,"E8")])],"isStart":true})]});Q9=makeQuery(id+"F10.opFillet","BLEND_EDGE",EDGE,{"blendedFrom":[makeQuery(id+"F9.boolean.opBoolean","INTERSECT",EDGE,{"derivedFrom":[subQ0,makeQuery(id+"F9.opExtrude","SWEPT_FACE",FACE,{"disambiguationData":[OSD([sQuery(id+"F8.wireOp",EDGE,"E11.7.0.0")])]})]}),makeQuery(id+"F9.boolean.opBoolean","INTERSECT",EDGE,{"derivedFrom":[subQ0,makeQuery(id+"F9.opExtrude","SWEPT_FACE",FACE,{"disambiguationData":[OSD([sQuery(id+"F8.wireOp",EDGE,"E11.7.0.4")])]})]})],"blendedInto":[]});}
            var Q10;
            {var subQ0=makeQuery(id+"F4.boolean.opBoolean","MERGE",FACE,{"derivedFrom":[makeQuery(id+"F1.opExtrude","CAP_FACE",FACE,{"disambiguationData":[OSD([sQuery(id+"F0.wireOp",EDGE,"E0.bottom"),sQuery(id+"F0.wireOp",EDGE,"E0.top"),sQuery(id+"F0.wireOp",EDGE,"E0.left"),sQuery(id+"F0.wireOp",EDGE,"E0.right"),sQuery(id+"F0.wireOp",EDGE,"E4"),sQuery(id+"F0.wireOp",EDGE,"E5")])],"isStart":false}),makeQuery(id+"F4.opExtrude","CAP_FACE",FACE,{"disambiguationData":[OSD([sQuery(id+"F3.wireOp",EDGE,"E6.0"),sQuery(id+"F3.wireOp",EDGE,"E7")])],"isStart":true}),makeQuery(id+"F4.opExtrude","CAP_FACE",FACE,{"disambiguationData":[OSD([sQuery(id+"F3.wireOp",EDGE,"E6.1"),sQuery(id+"F3.wireOp",EDGE,"E8")])],"isStart":true})]});Q10=makeQuery(id+"F10.opFillet","BLEND_EDGE",EDGE,{"blendedFrom":[makeQuery(id+"F9.boolean.opBoolean","INTERSECT",EDGE,{"derivedFrom":[subQ0,makeQuery(id+"F9.opExtrude","SWEPT_FACE",FACE,{"disambiguationData":[OSD([sQuery(id+"F8.wireOp",EDGE,"E11.7.0.1")])]})]}),makeQuery(id+"F9.boolean.opBoolean","INTERSECT",EDGE,{"derivedFrom":[subQ0,makeQuery(id+"F9.opExtrude","SWEPT_FACE",FACE,{"disambiguationData":[OSD([sQuery(id+"F8.wireOp",EDGE,"E11.7.0.4")])]})]})],"blendedInto":[]});}
            var Q11;
            {var subQ0=makeQuery(id+"F4.boolean.opBoolean","MERGE",FACE,{"derivedFrom":[makeQuery(id+"F1.opExtrude","CAP_FACE",FACE,{"disambiguationData":[OSD([sQuery(id+"F0.wireOp",EDGE,"E0.bottom"),sQuery(id+"F0.wireOp",EDGE,"E0.top"),sQuery(id+"F0.wireOp",EDGE,"E0.left"),sQuery(id+"F0.wireOp",EDGE,"E0.right"),sQuery(id+"F0.wireOp",EDGE,"E4"),sQuery(id+"F0.wireOp",EDGE,"E5")])],"isStart":false}),makeQuery(id+"F4.opExtrude","CAP_FACE",FACE,{"disambiguationData":[OSD([sQuery(id+"F3.wireOp",EDGE,"E6.0"),sQuery(id+"F3.wireOp",EDGE,"E7")])],"isStart":true}),makeQuery(id+"F4.opExtrude","CAP_FACE",FACE,{"disambiguationData":[OSD([sQuery(id+"F3.wireOp",EDGE,"E6.1"),sQuery(id+"F3.wireOp",EDGE,"E8")])],"isStart":true})]});Q11=makeQuery(id+"F10.opFillet","BLEND_EDGE",EDGE,{"blendedFrom":[makeQuery(id+"F9.boolean.opBoolean","INTERSECT",EDGE,{"derivedFrom":[subQ0,makeQuery(id+"F9.opExtrude","SWEPT_FACE",FACE,{"disambiguationData":[OSD([sQuery(id+"F8.wireOp",EDGE,"E11.7.0.1")])]})]}),makeQuery(id+"F9.boolean.opBoolean","INTERSECT",EDGE,{"derivedFrom":[subQ0,makeQuery(id+"F9.opExtrude","SWEPT_FACE",FACE,{"disambiguationData":[OSD([sQuery(id+"F8.wireOp",EDGE,"E11.7.0.2")])]})]})],"blendedInto":[]});}
            var Q12;
            {var subQ0=makeQuery(id+"F4.boolean.opBoolean","MERGE",FACE,{"derivedFrom":[makeQuery(id+"F1.opExtrude","CAP_FACE",FACE,{"disambiguationData":[OSD([sQuery(id+"F0.wireOp",EDGE,"E0.bottom"),sQuery(id+"F0.wireOp",EDGE,"E0.top"),sQuery(id+"F0.wireOp",EDGE,"E0.left"),sQuery(id+"F0.wireOp",EDGE,"E0.right"),sQuery(id+"F0.wireOp",EDGE,"E4"),sQuery(id+"F0.wireOp",EDGE,"E5")])],"isStart":false}),makeQuery(id+"F4.opExtrude","CAP_FACE",FACE,{"disambiguationData":[OSD([sQuery(id+"F3.wireOp",EDGE,"E6.0"),sQuery(id+"F3.wireOp",EDGE,"E7")])],"isStart":true}),makeQuery(id+"F4.opExtrude","CAP_FACE",FACE,{"disambiguationData":[OSD([sQuery(id+"F3.wireOp",EDGE,"E6.1"),sQuery(id+"F3.wireOp",EDGE,"E8")])],"isStart":true})]});Q12=makeQuery(id+"F10.opFillet","BLEND_EDGE",EDGE,{"blendedFrom":[makeQuery(id+"F9.boolean.opBoolean","INTERSECT",EDGE,{"derivedFrom":[subQ0,makeQuery(id+"F9.opExtrude","SWEPT_FACE",FACE,{"disambiguationData":[OSD([sQuery(id+"F8.wireOp",EDGE,"E11.6.0.0")])]})]}),makeQuery(id+"F9.boolean.opBoolean","INTERSECT",EDGE,{"derivedFrom":[subQ0,makeQuery(id+"F9.opExtrude","SWEPT_FACE",FACE,{"disambiguationData":[OSD([sQuery(id+"F8.wireOp",EDGE,"E11.6.0.2")])]})]})],"blendedInto":[]});}
            var Q13;
            {var subQ0=makeQuery(id+"F4.boolean.opBoolean","MERGE",FACE,{"derivedFrom":[makeQuery(id+"F1.opExtrude","CAP_FACE",FACE,{"disambiguationData":[OSD([sQuery(id+"F0.wireOp",EDGE,"E0.bottom"),sQuery(id+"F0.wireOp",EDGE,"E0.top"),sQuery(id+"F0.wireOp",EDGE,"E0.left"),sQuery(id+"F0.wireOp",EDGE,"E0.right"),sQuery(id+"F0.wireOp",EDGE,"E4"),sQuery(id+"F0.wireOp",EDGE,"E5")])],"isStart":false}),makeQuery(id+"F4.opExtrude","CAP_FACE",FACE,{"disambiguationData":[OSD([sQuery(id+"F3.wireOp",EDGE,"E6.0"),sQuery(id+"F3.wireOp",EDGE,"E7")])],"isStart":true}),makeQuery(id+"F4.opExtrude","CAP_FACE",FACE,{"disambiguationData":[OSD([sQuery(id+"F3.wireOp",EDGE,"E6.1"),sQuery(id+"F3.wireOp",EDGE,"E8")])],"isStart":true})]});Q13=makeQuery(id+"F10.opFillet","BLEND_EDGE",EDGE,{"blendedFrom":[makeQuery(id+"F9.boolean.opBoolean","INTERSECT",EDGE,{"derivedFrom":[subQ0,makeQuery(id+"F9.opExtrude","SWEPT_FACE",FACE,{"disambiguationData":[OSD([sQuery(id+"F8.wireOp",EDGE,"E11.6.0.0")])]})]}),makeQuery(id+"F9.boolean.opBoolean","INTERSECT",EDGE,{"derivedFrom":[subQ0,makeQuery(id+"F9.opExtrude","SWEPT_FACE",FACE,{"disambiguationData":[OSD([sQuery(id+"F8.wireOp",EDGE,"E11.6.0.4")])]})]})],"blendedInto":[]});}
            var Q14;
            {var subQ0=makeQuery(id+"F4.boolean.opBoolean","MERGE",FACE,{"derivedFrom":[makeQuery(id+"F1.opExtrude","CAP_FACE",FACE,{"disambiguationData":[OSD([sQuery(id+"F0.wireOp",EDGE,"E0.bottom"),sQuery(id+"F0.wireOp",EDGE,"E0.top"),sQuery(id+"F0.wireOp",EDGE,"E0.left"),sQuery(id+"F0.wireOp",EDGE,"E0.right"),sQuery(id+"F0.wireOp",EDGE,"E4"),sQuery(id+"F0.wireOp",EDGE,"E5")])],"isStart":false}),makeQuery(id+"F4.opExtrude","CAP_FACE",FACE,{"disambiguationData":[OSD([sQuery(id+"F3.wireOp",EDGE,"E6.0"),sQuery(id+"F3.wireOp",EDGE,"E7")])],"isStart":true}),makeQuery(id+"F4.opExtrude","CAP_FACE",FACE,{"disambiguationData":[OSD([sQuery(id+"F3.wireOp",EDGE,"E6.1"),sQuery(id+"F3.wireOp",EDGE,"E8")])],"isStart":true})]});Q14=makeQuery(id+"F10.opFillet","BLEND_EDGE",EDGE,{"blendedFrom":[makeQuery(id+"F9.boolean.opBoolean","INTERSECT",EDGE,{"derivedFrom":[subQ0,makeQuery(id+"F9.opExtrude","SWEPT_FACE",FACE,{"disambiguationData":[OSD([sQuery(id+"F8.wireOp",EDGE,"E11.6.0.1")])]})]}),makeQuery(id+"F9.boolean.opBoolean","INTERSECT",EDGE,{"derivedFrom":[subQ0,makeQuery(id+"F9.opExtrude","SWEPT_FACE",FACE,{"disambiguationData":[OSD([sQuery(id+"F8.wireOp",EDGE,"E11.6.0.2")])]})]})],"blendedInto":[]});}
            var Q15;
            {var subQ0=makeQuery(id+"F4.boolean.opBoolean","MERGE",FACE,{"derivedFrom":[makeQuery(id+"F1.opExtrude","CAP_FACE",FACE,{"disambiguationData":[OSD([sQuery(id+"F0.wireOp",EDGE,"E0.bottom"),sQuery(id+"F0.wireOp",EDGE,"E0.top"),sQuery(id+"F0.wireOp",EDGE,"E0.left"),sQuery(id+"F0.wireOp",EDGE,"E0.right"),sQuery(id+"F0.wireOp",EDGE,"E4"),sQuery(id+"F0.wireOp",EDGE,"E5")])],"isStart":false}),makeQuery(id+"F4.opExtrude","CAP_FACE",FACE,{"disambiguationData":[OSD([sQuery(id+"F3.wireOp",EDGE,"E6.0"),sQuery(id+"F3.wireOp",EDGE,"E7")])],"isStart":true}),makeQuery(id+"F4.opExtrude","CAP_FACE",FACE,{"disambiguationData":[OSD([sQuery(id+"F3.wireOp",EDGE,"E6.1"),sQuery(id+"F3.wireOp",EDGE,"E8")])],"isStart":true})]});Q15=makeQuery(id+"F10.opFillet","BLEND_EDGE",EDGE,{"blendedFrom":[makeQuery(id+"F9.boolean.opBoolean","INTERSECT",EDGE,{"derivedFrom":[subQ0,makeQuery(id+"F9.opExtrude","SWEPT_FACE",FACE,{"disambiguationData":[OSD([sQuery(id+"F8.wireOp",EDGE,"E11.6.0.1")])]})]}),makeQuery(id+"F9.boolean.opBoolean","INTERSECT",EDGE,{"derivedFrom":[subQ0,makeQuery(id+"F9.opExtrude","SWEPT_FACE",FACE,{"disambiguationData":[OSD([sQuery(id+"F8.wireOp",EDGE,"E11.6.0.4")])]})]})],"blendedInto":[]});}
            var Q16;
            {var subQ0=makeQuery(id+"F4.boolean.opBoolean","MERGE",FACE,{"derivedFrom":[makeQuery(id+"F1.opExtrude","CAP_FACE",FACE,{"disambiguationData":[OSD([sQuery(id+"F0.wireOp",EDGE,"E0.bottom"),sQuery(id+"F0.wireOp",EDGE,"E0.top"),sQuery(id+"F0.wireOp",EDGE,"E0.left"),sQuery(id+"F0.wireOp",EDGE,"E0.right"),sQuery(id+"F0.wireOp",EDGE,"E4"),sQuery(id+"F0.wireOp",EDGE,"E5")])],"isStart":false}),makeQuery(id+"F4.opExtrude","CAP_FACE",FACE,{"disambiguationData":[OSD([sQuery(id+"F3.wireOp",EDGE,"E6.0"),sQuery(id+"F3.wireOp",EDGE,"E7")])],"isStart":true}),makeQuery(id+"F4.opExtrude","CAP_FACE",FACE,{"disambiguationData":[OSD([sQuery(id+"F3.wireOp",EDGE,"E6.1"),sQuery(id+"F3.wireOp",EDGE,"E8")])],"isStart":true})]});Q16=makeQuery(id+"F10.opFillet","BLEND_EDGE",EDGE,{"blendedFrom":[makeQuery(id+"F9.boolean.opBoolean","INTERSECT",EDGE,{"derivedFrom":[subQ0,makeQuery(id+"F9.opExtrude","SWEPT_FACE",FACE,{"disambiguationData":[OSD([sQuery(id+"F8.wireOp",EDGE,"E11.5.0.0")])]})]}),makeQuery(id+"F9.boolean.opBoolean","INTERSECT",EDGE,{"derivedFrom":[subQ0,makeQuery(id+"F9.opExtrude","SWEPT_FACE",FACE,{"disambiguationData":[OSD([sQuery(id+"F8.wireOp",EDGE,"E11.5.0.4")])]})]})],"blendedInto":[]});}
            var Q17;
            {var subQ0=makeQuery(id+"F4.boolean.opBoolean","MERGE",FACE,{"derivedFrom":[makeQuery(id+"F1.opExtrude","CAP_FACE",FACE,{"disambiguationData":[OSD([sQuery(id+"F0.wireOp",EDGE,"E0.bottom"),sQuery(id+"F0.wireOp",EDGE,"E0.top"),sQuery(id+"F0.wireOp",EDGE,"E0.left"),sQuery(id+"F0.wireOp",EDGE,"E0.right"),sQuery(id+"F0.wireOp",EDGE,"E4"),sQuery(id+"F0.wireOp",EDGE,"E5")])],"isStart":false}),makeQuery(id+"F4.opExtrude","CAP_FACE",FACE,{"disambiguationData":[OSD([sQuery(id+"F3.wireOp",EDGE,"E6.0"),sQuery(id+"F3.wireOp",EDGE,"E7")])],"isStart":true}),makeQuery(id+"F4.opExtrude","CAP_FACE",FACE,{"disambiguationData":[OSD([sQuery(id+"F3.wireOp",EDGE,"E6.1"),sQuery(id+"F3.wireOp",EDGE,"E8")])],"isStart":true})]});Q17=makeQuery(id+"F10.opFillet","BLEND_EDGE",EDGE,{"blendedFrom":[makeQuery(id+"F9.boolean.opBoolean","INTERSECT",EDGE,{"derivedFrom":[subQ0,makeQuery(id+"F9.opExtrude","SWEPT_FACE",FACE,{"disambiguationData":[OSD([sQuery(id+"F8.wireOp",EDGE,"E11.5.0.0")])]})]}),makeQuery(id+"F9.boolean.opBoolean","INTERSECT",EDGE,{"derivedFrom":[subQ0,makeQuery(id+"F9.opExtrude","SWEPT_FACE",FACE,{"disambiguationData":[OSD([sQuery(id+"F8.wireOp",EDGE,"E11.5.0.2")])]})]})],"blendedInto":[]});}
            var Q18;
            {var subQ0=makeQuery(id+"F4.boolean.opBoolean","MERGE",FACE,{"derivedFrom":[makeQuery(id+"F1.opExtrude","CAP_FACE",FACE,{"disambiguationData":[OSD([sQuery(id+"F0.wireOp",EDGE,"E0.bottom"),sQuery(id+"F0.wireOp",EDGE,"E0.top"),sQuery(id+"F0.wireOp",EDGE,"E0.left"),sQuery(id+"F0.wireOp",EDGE,"E0.right"),sQuery(id+"F0.wireOp",EDGE,"E4"),sQuery(id+"F0.wireOp",EDGE,"E5")])],"isStart":false}),makeQuery(id+"F4.opExtrude","CAP_FACE",FACE,{"disambiguationData":[OSD([sQuery(id+"F3.wireOp",EDGE,"E6.0"),sQuery(id+"F3.wireOp",EDGE,"E7")])],"isStart":true}),makeQuery(id+"F4.opExtrude","CAP_FACE",FACE,{"disambiguationData":[OSD([sQuery(id+"F3.wireOp",EDGE,"E6.1"),sQuery(id+"F3.wireOp",EDGE,"E8")])],"isStart":true})]});Q18=makeQuery(id+"F10.opFillet","BLEND_EDGE",EDGE,{"blendedFrom":[makeQuery(id+"F9.boolean.opBoolean","INTERSECT",EDGE,{"derivedFrom":[subQ0,makeQuery(id+"F9.opExtrude","SWEPT_FACE",FACE,{"disambiguationData":[OSD([sQuery(id+"F8.wireOp",EDGE,"E11.5.0.1")])]})]}),makeQuery(id+"F9.boolean.opBoolean","INTERSECT",EDGE,{"derivedFrom":[subQ0,makeQuery(id+"F9.opExtrude","SWEPT_FACE",FACE,{"disambiguationData":[OSD([sQuery(id+"F8.wireOp",EDGE,"E11.5.0.2")])]})]})],"blendedInto":[]});}
            var Q19;
            {var subQ0=makeQuery(id+"F4.boolean.opBoolean","MERGE",FACE,{"derivedFrom":[makeQuery(id+"F1.opExtrude","CAP_FACE",FACE,{"disambiguationData":[OSD([sQuery(id+"F0.wireOp",EDGE,"E0.bottom"),sQuery(id+"F0.wireOp",EDGE,"E0.top"),sQuery(id+"F0.wireOp",EDGE,"E0.left"),sQuery(id+"F0.wireOp",EDGE,"E0.right"),sQuery(id+"F0.wireOp",EDGE,"E4"),sQuery(id+"F0.wireOp",EDGE,"E5")])],"isStart":false}),makeQuery(id+"F4.opExtrude","CAP_FACE",FACE,{"disambiguationData":[OSD([sQuery(id+"F3.wireOp",EDGE,"E6.0"),sQuery(id+"F3.wireOp",EDGE,"E7")])],"isStart":true}),makeQuery(id+"F4.opExtrude","CAP_FACE",FACE,{"disambiguationData":[OSD([sQuery(id+"F3.wireOp",EDGE,"E6.1"),sQuery(id+"F3.wireOp",EDGE,"E8")])],"isStart":true})]});Q19=makeQuery(id+"F10.opFillet","BLEND_EDGE",EDGE,{"blendedFrom":[makeQuery(id+"F9.boolean.opBoolean","INTERSECT",EDGE,{"derivedFrom":[subQ0,makeQuery(id+"F9.opExtrude","SWEPT_FACE",FACE,{"disambiguationData":[OSD([sQuery(id+"F8.wireOp",EDGE,"E11.5.0.1")])]})]}),makeQuery(id+"F9.boolean.opBoolean","INTERSECT",EDGE,{"derivedFrom":[subQ0,makeQuery(id+"F9.opExtrude","SWEPT_FACE",FACE,{"disambiguationData":[OSD([sQuery(id+"F8.wireOp",EDGE,"E11.5.0.4")])]})]})],"blendedInto":[]});}
            var Q20;
            {var subQ0=makeQuery(id+"F4.boolean.opBoolean","MERGE",FACE,{"derivedFrom":[makeQuery(id+"F1.opExtrude","CAP_FACE",FACE,{"disambiguationData":[OSD([sQuery(id+"F0.wireOp",EDGE,"E0.bottom"),sQuery(id+"F0.wireOp",EDGE,"E0.top"),sQuery(id+"F0.wireOp",EDGE,"E0.left"),sQuery(id+"F0.wireOp",EDGE,"E0.right"),sQuery(id+"F0.wireOp",EDGE,"E4"),sQuery(id+"F0.wireOp",EDGE,"E5")])],"isStart":false}),makeQuery(id+"F4.opExtrude","CAP_FACE",FACE,{"disambiguationData":[OSD([sQuery(id+"F3.wireOp",EDGE,"E6.0"),sQuery(id+"F3.wireOp",EDGE,"E7")])],"isStart":true}),makeQuery(id+"F4.opExtrude","CAP_FACE",FACE,{"disambiguationData":[OSD([sQuery(id+"F3.wireOp",EDGE,"E6.1"),sQuery(id+"F3.wireOp",EDGE,"E8")])],"isStart":true})]});Q20=makeQuery(id+"F10.opFillet","BLEND_EDGE",EDGE,{"blendedFrom":[makeQuery(id+"F9.boolean.opBoolean","INTERSECT",EDGE,{"derivedFrom":[subQ0,makeQuery(id+"F9.opExtrude","SWEPT_FACE",FACE,{"disambiguationData":[OSD([sQuery(id+"F8.wireOp",EDGE,"E11.4.0.0")])]})]}),makeQuery(id+"F9.boolean.opBoolean","INTERSECT",EDGE,{"derivedFrom":[subQ0,makeQuery(id+"F9.opExtrude","SWEPT_FACE",FACE,{"disambiguationData":[OSD([sQuery(id+"F8.wireOp",EDGE,"E11.4.0.4")])]})]})],"blendedInto":[]});}
            var Q21;
            {var subQ0=makeQuery(id+"F4.boolean.opBoolean","MERGE",FACE,{"derivedFrom":[makeQuery(id+"F1.opExtrude","CAP_FACE",FACE,{"disambiguationData":[OSD([sQuery(id+"F0.wireOp",EDGE,"E0.bottom"),sQuery(id+"F0.wireOp",EDGE,"E0.top"),sQuery(id+"F0.wireOp",EDGE,"E0.left"),sQuery(id+"F0.wireOp",EDGE,"E0.right"),sQuery(id+"F0.wireOp",EDGE,"E4"),sQuery(id+"F0.wireOp",EDGE,"E5")])],"isStart":false}),makeQuery(id+"F4.opExtrude","CAP_FACE",FACE,{"disambiguationData":[OSD([sQuery(id+"F3.wireOp",EDGE,"E6.0"),sQuery(id+"F3.wireOp",EDGE,"E7")])],"isStart":true}),makeQuery(id+"F4.opExtrude","CAP_FACE",FACE,{"disambiguationData":[OSD([sQuery(id+"F3.wireOp",EDGE,"E6.1"),sQuery(id+"F3.wireOp",EDGE,"E8")])],"isStart":true})]});Q21=makeQuery(id+"F10.opFillet","BLEND_EDGE",EDGE,{"blendedFrom":[makeQuery(id+"F9.boolean.opBoolean","INTERSECT",EDGE,{"derivedFrom":[subQ0,makeQuery(id+"F9.opExtrude","SWEPT_FACE",FACE,{"disambiguationData":[OSD([sQuery(id+"F8.wireOp",EDGE,"E11.4.0.0")])]})]}),makeQuery(id+"F9.boolean.opBoolean","INTERSECT",EDGE,{"derivedFrom":[subQ0,makeQuery(id+"F9.opExtrude","SWEPT_FACE",FACE,{"disambiguationData":[OSD([sQuery(id+"F8.wireOp",EDGE,"E11.4.0.2")])]})]})],"blendedInto":[]});}
            var Q22;
            {var subQ0=makeQuery(id+"F4.boolean.opBoolean","MERGE",FACE,{"derivedFrom":[makeQuery(id+"F1.opExtrude","CAP_FACE",FACE,{"disambiguationData":[OSD([sQuery(id+"F0.wireOp",EDGE,"E0.bottom"),sQuery(id+"F0.wireOp",EDGE,"E0.top"),sQuery(id+"F0.wireOp",EDGE,"E0.left"),sQuery(id+"F0.wireOp",EDGE,"E0.right"),sQuery(id+"F0.wireOp",EDGE,"E4"),sQuery(id+"F0.wireOp",EDGE,"E5")])],"isStart":false}),makeQuery(id+"F4.opExtrude","CAP_FACE",FACE,{"disambiguationData":[OSD([sQuery(id+"F3.wireOp",EDGE,"E6.0"),sQuery(id+"F3.wireOp",EDGE,"E7")])],"isStart":true}),makeQuery(id+"F4.opExtrude","CAP_FACE",FACE,{"disambiguationData":[OSD([sQuery(id+"F3.wireOp",EDGE,"E6.1"),sQuery(id+"F3.wireOp",EDGE,"E8")])],"isStart":true})]});Q22=makeQuery(id+"F10.opFillet","BLEND_EDGE",EDGE,{"blendedFrom":[makeQuery(id+"F9.boolean.opBoolean","INTERSECT",EDGE,{"derivedFrom":[subQ0,makeQuery(id+"F9.opExtrude","SWEPT_FACE",FACE,{"disambiguationData":[OSD([sQuery(id+"F8.wireOp",EDGE,"E11.4.0.1")])]})]}),makeQuery(id+"F9.boolean.opBoolean","INTERSECT",EDGE,{"derivedFrom":[subQ0,makeQuery(id+"F9.opExtrude","SWEPT_FACE",FACE,{"disambiguationData":[OSD([sQuery(id+"F8.wireOp",EDGE,"E11.4.0.2")])]})]})],"blendedInto":[]});}
            var Q23;
            {var subQ0=makeQuery(id+"F4.boolean.opBoolean","MERGE",FACE,{"derivedFrom":[makeQuery(id+"F1.opExtrude","CAP_FACE",FACE,{"disambiguationData":[OSD([sQuery(id+"F0.wireOp",EDGE,"E0.bottom"),sQuery(id+"F0.wireOp",EDGE,"E0.top"),sQuery(id+"F0.wireOp",EDGE,"E0.left"),sQuery(id+"F0.wireOp",EDGE,"E0.right"),sQuery(id+"F0.wireOp",EDGE,"E4"),sQuery(id+"F0.wireOp",EDGE,"E5")])],"isStart":false}),makeQuery(id+"F4.opExtrude","CAP_FACE",FACE,{"disambiguationData":[OSD([sQuery(id+"F3.wireOp",EDGE,"E6.0"),sQuery(id+"F3.wireOp",EDGE,"E7")])],"isStart":true}),makeQuery(id+"F4.opExtrude","CAP_FACE",FACE,{"disambiguationData":[OSD([sQuery(id+"F3.wireOp",EDGE,"E6.1"),sQuery(id+"F3.wireOp",EDGE,"E8")])],"isStart":true})]});Q23=makeQuery(id+"F10.opFillet","BLEND_EDGE",EDGE,{"blendedFrom":[makeQuery(id+"F9.boolean.opBoolean","INTERSECT",EDGE,{"derivedFrom":[subQ0,makeQuery(id+"F9.opExtrude","SWEPT_FACE",FACE,{"disambiguationData":[OSD([sQuery(id+"F8.wireOp",EDGE,"E11.4.0.1")])]})]}),makeQuery(id+"F9.boolean.opBoolean","INTERSECT",EDGE,{"derivedFrom":[subQ0,makeQuery(id+"F9.opExtrude","SWEPT_FACE",FACE,{"disambiguationData":[OSD([sQuery(id+"F8.wireOp",EDGE,"E11.4.0.4")])]})]})],"blendedInto":[]});}
            var Q24;
            {var subQ0=makeQuery(id+"F4.boolean.opBoolean","MERGE",FACE,{"derivedFrom":[makeQuery(id+"F1.opExtrude","CAP_FACE",FACE,{"disambiguationData":[OSD([sQuery(id+"F0.wireOp",EDGE,"E0.bottom"),sQuery(id+"F0.wireOp",EDGE,"E0.top"),sQuery(id+"F0.wireOp",EDGE,"E0.left"),sQuery(id+"F0.wireOp",EDGE,"E0.right"),sQuery(id+"F0.wireOp",EDGE,"E4"),sQuery(id+"F0.wireOp",EDGE,"E5")])],"isStart":false}),makeQuery(id+"F4.opExtrude","CAP_FACE",FACE,{"disambiguationData":[OSD([sQuery(id+"F3.wireOp",EDGE,"E6.0"),sQuery(id+"F3.wireOp",EDGE,"E7")])],"isStart":true}),makeQuery(id+"F4.opExtrude","CAP_FACE",FACE,{"disambiguationData":[OSD([sQuery(id+"F3.wireOp",EDGE,"E6.1"),sQuery(id+"F3.wireOp",EDGE,"E8")])],"isStart":true})]});Q24=makeQuery(id+"F10.opFillet","BLEND_EDGE",EDGE,{"blendedFrom":[makeQuery(id+"F9.boolean.opBoolean","INTERSECT",EDGE,{"derivedFrom":[subQ0,makeQuery(id+"F9.opExtrude","SWEPT_FACE",FACE,{"disambiguationData":[OSD([sQuery(id+"F8.wireOp",EDGE,"E11.3.0.0")])]})]}),makeQuery(id+"F9.boolean.opBoolean","INTERSECT",EDGE,{"derivedFrom":[subQ0,makeQuery(id+"F9.opExtrude","SWEPT_FACE",FACE,{"disambiguationData":[OSD([sQuery(id+"F8.wireOp",EDGE,"E11.3.0.4")])]})]})],"blendedInto":[]});}
            var Q25;
            {var subQ0=makeQuery(id+"F4.boolean.opBoolean","MERGE",FACE,{"derivedFrom":[makeQuery(id+"F1.opExtrude","CAP_FACE",FACE,{"disambiguationData":[OSD([sQuery(id+"F0.wireOp",EDGE,"E0.bottom"),sQuery(id+"F0.wireOp",EDGE,"E0.top"),sQuery(id+"F0.wireOp",EDGE,"E0.left"),sQuery(id+"F0.wireOp",EDGE,"E0.right"),sQuery(id+"F0.wireOp",EDGE,"E4"),sQuery(id+"F0.wireOp",EDGE,"E5")])],"isStart":false}),makeQuery(id+"F4.opExtrude","CAP_FACE",FACE,{"disambiguationData":[OSD([sQuery(id+"F3.wireOp",EDGE,"E6.0"),sQuery(id+"F3.wireOp",EDGE,"E7")])],"isStart":true}),makeQuery(id+"F4.opExtrude","CAP_FACE",FACE,{"disambiguationData":[OSD([sQuery(id+"F3.wireOp",EDGE,"E6.1"),sQuery(id+"F3.wireOp",EDGE,"E8")])],"isStart":true})]});Q25=makeQuery(id+"F10.opFillet","BLEND_EDGE",EDGE,{"blendedFrom":[makeQuery(id+"F9.boolean.opBoolean","INTERSECT",EDGE,{"derivedFrom":[subQ0,makeQuery(id+"F9.opExtrude","SWEPT_FACE",FACE,{"disambiguationData":[OSD([sQuery(id+"F8.wireOp",EDGE,"E11.3.0.1")])]})]}),makeQuery(id+"F9.boolean.opBoolean","INTERSECT",EDGE,{"derivedFrom":[subQ0,makeQuery(id+"F9.opExtrude","SWEPT_FACE",FACE,{"disambiguationData":[OSD([sQuery(id+"F8.wireOp",EDGE,"E11.3.0.4")])]})]})],"blendedInto":[]});}
            var Q26;
            {var subQ0=makeQuery(id+"F4.boolean.opBoolean","MERGE",FACE,{"derivedFrom":[makeQuery(id+"F1.opExtrude","CAP_FACE",FACE,{"disambiguationData":[OSD([sQuery(id+"F0.wireOp",EDGE,"E0.bottom"),sQuery(id+"F0.wireOp",EDGE,"E0.top"),sQuery(id+"F0.wireOp",EDGE,"E0.left"),sQuery(id+"F0.wireOp",EDGE,"E0.right"),sQuery(id+"F0.wireOp",EDGE,"E4"),sQuery(id+"F0.wireOp",EDGE,"E5")])],"isStart":false}),makeQuery(id+"F4.opExtrude","CAP_FACE",FACE,{"disambiguationData":[OSD([sQuery(id+"F3.wireOp",EDGE,"E6.0"),sQuery(id+"F3.wireOp",EDGE,"E7")])],"isStart":true}),makeQuery(id+"F4.opExtrude","CAP_FACE",FACE,{"disambiguationData":[OSD([sQuery(id+"F3.wireOp",EDGE,"E6.1"),sQuery(id+"F3.wireOp",EDGE,"E8")])],"isStart":true})]});Q26=makeQuery(id+"F10.opFillet","BLEND_EDGE",EDGE,{"blendedFrom":[makeQuery(id+"F9.boolean.opBoolean","INTERSECT",EDGE,{"derivedFrom":[subQ0,makeQuery(id+"F9.opExtrude","SWEPT_FACE",FACE,{"disambiguationData":[OSD([sQuery(id+"F8.wireOp",EDGE,"E11.3.0.1")])]})]}),makeQuery(id+"F9.boolean.opBoolean","INTERSECT",EDGE,{"derivedFrom":[subQ0,makeQuery(id+"F9.opExtrude","SWEPT_FACE",FACE,{"disambiguationData":[OSD([sQuery(id+"F8.wireOp",EDGE,"E11.3.0.2")])]})]})],"blendedInto":[]});}
            var Q27;
            {var subQ0=makeQuery(id+"F4.boolean.opBoolean","MERGE",FACE,{"derivedFrom":[makeQuery(id+"F1.opExtrude","CAP_FACE",FACE,{"disambiguationData":[OSD([sQuery(id+"F0.wireOp",EDGE,"E0.bottom"),sQuery(id+"F0.wireOp",EDGE,"E0.top"),sQuery(id+"F0.wireOp",EDGE,"E0.left"),sQuery(id+"F0.wireOp",EDGE,"E0.right"),sQuery(id+"F0.wireOp",EDGE,"E4"),sQuery(id+"F0.wireOp",EDGE,"E5")])],"isStart":false}),makeQuery(id+"F4.opExtrude","CAP_FACE",FACE,{"disambiguationData":[OSD([sQuery(id+"F3.wireOp",EDGE,"E6.0"),sQuery(id+"F3.wireOp",EDGE,"E7")])],"isStart":true}),makeQuery(id+"F4.opExtrude","CAP_FACE",FACE,{"disambiguationData":[OSD([sQuery(id+"F3.wireOp",EDGE,"E6.1"),sQuery(id+"F3.wireOp",EDGE,"E8")])],"isStart":true})]});Q27=makeQuery(id+"F10.opFillet","BLEND_EDGE",EDGE,{"blendedFrom":[makeQuery(id+"F9.boolean.opBoolean","INTERSECT",EDGE,{"derivedFrom":[subQ0,makeQuery(id+"F9.opExtrude","SWEPT_FACE",FACE,{"disambiguationData":[OSD([sQuery(id+"F8.wireOp",EDGE,"E11.3.0.0")])]})]}),makeQuery(id+"F9.boolean.opBoolean","INTERSECT",EDGE,{"derivedFrom":[subQ0,makeQuery(id+"F9.opExtrude","SWEPT_FACE",FACE,{"disambiguationData":[OSD([sQuery(id+"F8.wireOp",EDGE,"E11.3.0.2")])]})]})],"blendedInto":[]});}
            var Q28;
            {var subQ0=makeQuery(id+"F4.boolean.opBoolean","MERGE",FACE,{"derivedFrom":[makeQuery(id+"F1.opExtrude","CAP_FACE",FACE,{"disambiguationData":[OSD([sQuery(id+"F0.wireOp",EDGE,"E0.bottom"),sQuery(id+"F0.wireOp",EDGE,"E0.top"),sQuery(id+"F0.wireOp",EDGE,"E0.left"),sQuery(id+"F0.wireOp",EDGE,"E0.right"),sQuery(id+"F0.wireOp",EDGE,"E4"),sQuery(id+"F0.wireOp",EDGE,"E5")])],"isStart":false}),makeQuery(id+"F4.opExtrude","CAP_FACE",FACE,{"disambiguationData":[OSD([sQuery(id+"F3.wireOp",EDGE,"E6.0"),sQuery(id+"F3.wireOp",EDGE,"E7")])],"isStart":true}),makeQuery(id+"F4.opExtrude","CAP_FACE",FACE,{"disambiguationData":[OSD([sQuery(id+"F3.wireOp",EDGE,"E6.1"),sQuery(id+"F3.wireOp",EDGE,"E8")])],"isStart":true})]});Q28=makeQuery(id+"F10.opFillet","BLEND_EDGE",EDGE,{"blendedFrom":[makeQuery(id+"F9.boolean.opBoolean","INTERSECT",EDGE,{"derivedFrom":[subQ0,makeQuery(id+"F9.opExtrude","SWEPT_FACE",FACE,{"disambiguationData":[OSD([sQuery(id+"F8.wireOp",EDGE,"E11.2.0.1")])]})]}),makeQuery(id+"F9.boolean.opBoolean","INTERSECT",EDGE,{"derivedFrom":[subQ0,makeQuery(id+"F9.opExtrude","SWEPT_FACE",FACE,{"disambiguationData":[OSD([sQuery(id+"F8.wireOp",EDGE,"E11.2.0.2")])]})]})],"blendedInto":[]});}
            var Q29;
            {var subQ0=makeQuery(id+"F4.boolean.opBoolean","MERGE",FACE,{"derivedFrom":[makeQuery(id+"F1.opExtrude","CAP_FACE",FACE,{"disambiguationData":[OSD([sQuery(id+"F0.wireOp",EDGE,"E0.bottom"),sQuery(id+"F0.wireOp",EDGE,"E0.top"),sQuery(id+"F0.wireOp",EDGE,"E0.left"),sQuery(id+"F0.wireOp",EDGE,"E0.right"),sQuery(id+"F0.wireOp",EDGE,"E4"),sQuery(id+"F0.wireOp",EDGE,"E5")])],"isStart":false}),makeQuery(id+"F4.opExtrude","CAP_FACE",FACE,{"disambiguationData":[OSD([sQuery(id+"F3.wireOp",EDGE,"E6.0"),sQuery(id+"F3.wireOp",EDGE,"E7")])],"isStart":true}),makeQuery(id+"F4.opExtrude","CAP_FACE",FACE,{"disambiguationData":[OSD([sQuery(id+"F3.wireOp",EDGE,"E6.1"),sQuery(id+"F3.wireOp",EDGE,"E8")])],"isStart":true})]});Q29=makeQuery(id+"F10.opFillet","BLEND_EDGE",EDGE,{"blendedFrom":[makeQuery(id+"F9.boolean.opBoolean","INTERSECT",EDGE,{"derivedFrom":[subQ0,makeQuery(id+"F9.opExtrude","SWEPT_FACE",FACE,{"disambiguationData":[OSD([sQuery(id+"F8.wireOp",EDGE,"E11.2.0.0")])]})]}),makeQuery(id+"F9.boolean.opBoolean","INTERSECT",EDGE,{"derivedFrom":[subQ0,makeQuery(id+"F9.opExtrude","SWEPT_FACE",FACE,{"disambiguationData":[OSD([sQuery(id+"F8.wireOp",EDGE,"E11.2.0.2")])]})]})],"blendedInto":[]});}
            var Q30;
            {var subQ0=makeQuery(id+"F4.boolean.opBoolean","MERGE",FACE,{"derivedFrom":[makeQuery(id+"F1.opExtrude","CAP_FACE",FACE,{"disambiguationData":[OSD([sQuery(id+"F0.wireOp",EDGE,"E0.bottom"),sQuery(id+"F0.wireOp",EDGE,"E0.top"),sQuery(id+"F0.wireOp",EDGE,"E0.left"),sQuery(id+"F0.wireOp",EDGE,"E0.right"),sQuery(id+"F0.wireOp",EDGE,"E4"),sQuery(id+"F0.wireOp",EDGE,"E5")])],"isStart":false}),makeQuery(id+"F4.opExtrude","CAP_FACE",FACE,{"disambiguationData":[OSD([sQuery(id+"F3.wireOp",EDGE,"E6.0"),sQuery(id+"F3.wireOp",EDGE,"E7")])],"isStart":true}),makeQuery(id+"F4.opExtrude","CAP_FACE",FACE,{"disambiguationData":[OSD([sQuery(id+"F3.wireOp",EDGE,"E6.1"),sQuery(id+"F3.wireOp",EDGE,"E8")])],"isStart":true})]});Q30=makeQuery(id+"F10.opFillet","BLEND_EDGE",EDGE,{"blendedFrom":[makeQuery(id+"F9.boolean.opBoolean","INTERSECT",EDGE,{"derivedFrom":[subQ0,makeQuery(id+"F9.opExtrude","SWEPT_FACE",FACE,{"disambiguationData":[OSD([sQuery(id+"F8.wireOp",EDGE,"E11.2.0.0")])]})]}),makeQuery(id+"F9.boolean.opBoolean","INTERSECT",EDGE,{"derivedFrom":[subQ0,makeQuery(id+"F9.opExtrude","SWEPT_FACE",FACE,{"disambiguationData":[OSD([sQuery(id+"F8.wireOp",EDGE,"E11.2.0.4")])]})]})],"blendedInto":[]});}
            var Q31;
            {var subQ0=makeQuery(id+"F4.boolean.opBoolean","MERGE",FACE,{"derivedFrom":[makeQuery(id+"F1.opExtrude","CAP_FACE",FACE,{"disambiguationData":[OSD([sQuery(id+"F0.wireOp",EDGE,"E0.bottom"),sQuery(id+"F0.wireOp",EDGE,"E0.top"),sQuery(id+"F0.wireOp",EDGE,"E0.left"),sQuery(id+"F0.wireOp",EDGE,"E0.right"),sQuery(id+"F0.wireOp",EDGE,"E4"),sQuery(id+"F0.wireOp",EDGE,"E5")])],"isStart":false}),makeQuery(id+"F4.opExtrude","CAP_FACE",FACE,{"disambiguationData":[OSD([sQuery(id+"F3.wireOp",EDGE,"E6.0"),sQuery(id+"F3.wireOp",EDGE,"E7")])],"isStart":true}),makeQuery(id+"F4.opExtrude","CAP_FACE",FACE,{"disambiguationData":[OSD([sQuery(id+"F3.wireOp",EDGE,"E6.1"),sQuery(id+"F3.wireOp",EDGE,"E8")])],"isStart":true})]});Q31=makeQuery(id+"F10.opFillet","BLEND_EDGE",EDGE,{"blendedFrom":[makeQuery(id+"F9.boolean.opBoolean","INTERSECT",EDGE,{"derivedFrom":[subQ0,makeQuery(id+"F9.opExtrude","SWEPT_FACE",FACE,{"disambiguationData":[OSD([sQuery(id+"F8.wireOp",EDGE,"E11.2.0.1")])]})]}),makeQuery(id+"F9.boolean.opBoolean","INTERSECT",EDGE,{"derivedFrom":[subQ0,makeQuery(id+"F9.opExtrude","SWEPT_FACE",FACE,{"disambiguationData":[OSD([sQuery(id+"F8.wireOp",EDGE,"E11.2.0.4")])]})]})],"blendedInto":[]});}
            var Q32;
            {var subQ0=makeQuery(id+"F4.boolean.opBoolean","MERGE",FACE,{"derivedFrom":[makeQuery(id+"F1.opExtrude","CAP_FACE",FACE,{"disambiguationData":[OSD([sQuery(id+"F0.wireOp",EDGE,"E0.bottom"),sQuery(id+"F0.wireOp",EDGE,"E0.top"),sQuery(id+"F0.wireOp",EDGE,"E0.left"),sQuery(id+"F0.wireOp",EDGE,"E0.right"),sQuery(id+"F0.wireOp",EDGE,"E4"),sQuery(id+"F0.wireOp",EDGE,"E5")])],"isStart":false}),makeQuery(id+"F4.opExtrude","CAP_FACE",FACE,{"disambiguationData":[OSD([sQuery(id+"F3.wireOp",EDGE,"E6.0"),sQuery(id+"F3.wireOp",EDGE,"E7")])],"isStart":true}),makeQuery(id+"F4.opExtrude","CAP_FACE",FACE,{"disambiguationData":[OSD([sQuery(id+"F3.wireOp",EDGE,"E6.1"),sQuery(id+"F3.wireOp",EDGE,"E8")])],"isStart":true})]});Q32=makeQuery(id+"F10.opFillet","BLEND_EDGE",EDGE,{"blendedFrom":[makeQuery(id+"F9.boolean.opBoolean","INTERSECT",EDGE,{"derivedFrom":[subQ0,makeQuery(id+"F9.opExtrude","SWEPT_FACE",FACE,{"disambiguationData":[OSD([sQuery(id+"F8.wireOp",EDGE,"E11.1.0.1")])]})]}),makeQuery(id+"F9.boolean.opBoolean","INTERSECT",EDGE,{"derivedFrom":[subQ0,makeQuery(id+"F9.opExtrude","SWEPT_FACE",FACE,{"disambiguationData":[OSD([sQuery(id+"F8.wireOp",EDGE,"E11.1.0.4")])]})]})],"blendedInto":[]});}
            var Q33;
            {var subQ0=makeQuery(id+"F4.boolean.opBoolean","MERGE",FACE,{"derivedFrom":[makeQuery(id+"F1.opExtrude","CAP_FACE",FACE,{"disambiguationData":[OSD([sQuery(id+"F0.wireOp",EDGE,"E0.bottom"),sQuery(id+"F0.wireOp",EDGE,"E0.top"),sQuery(id+"F0.wireOp",EDGE,"E0.left"),sQuery(id+"F0.wireOp",EDGE,"E0.right"),sQuery(id+"F0.wireOp",EDGE,"E4"),sQuery(id+"F0.wireOp",EDGE,"E5")])],"isStart":false}),makeQuery(id+"F4.opExtrude","CAP_FACE",FACE,{"disambiguationData":[OSD([sQuery(id+"F3.wireOp",EDGE,"E6.0"),sQuery(id+"F3.wireOp",EDGE,"E7")])],"isStart":true}),makeQuery(id+"F4.opExtrude","CAP_FACE",FACE,{"disambiguationData":[OSD([sQuery(id+"F3.wireOp",EDGE,"E6.1"),sQuery(id+"F3.wireOp",EDGE,"E8")])],"isStart":true})]});Q33=makeQuery(id+"F10.opFillet","BLEND_EDGE",EDGE,{"blendedFrom":[makeQuery(id+"F9.boolean.opBoolean","INTERSECT",EDGE,{"derivedFrom":[subQ0,makeQuery(id+"F9.opExtrude","SWEPT_FACE",FACE,{"disambiguationData":[OSD([sQuery(id+"F8.wireOp",EDGE,"E11.1.0.1")])]})]}),makeQuery(id+"F9.boolean.opBoolean","INTERSECT",EDGE,{"derivedFrom":[subQ0,makeQuery(id+"F9.opExtrude","SWEPT_FACE",FACE,{"disambiguationData":[OSD([sQuery(id+"F8.wireOp",EDGE,"E11.1.0.2")])]})]})],"blendedInto":[]});}
            var Q34;
            {var subQ0=makeQuery(id+"F4.boolean.opBoolean","MERGE",FACE,{"derivedFrom":[makeQuery(id+"F1.opExtrude","CAP_FACE",FACE,{"disambiguationData":[OSD([sQuery(id+"F0.wireOp",EDGE,"E0.bottom"),sQuery(id+"F0.wireOp",EDGE,"E0.top"),sQuery(id+"F0.wireOp",EDGE,"E0.left"),sQuery(id+"F0.wireOp",EDGE,"E0.right"),sQuery(id+"F0.wireOp",EDGE,"E4"),sQuery(id+"F0.wireOp",EDGE,"E5")])],"isStart":false}),makeQuery(id+"F4.opExtrude","CAP_FACE",FACE,{"disambiguationData":[OSD([sQuery(id+"F3.wireOp",EDGE,"E6.0"),sQuery(id+"F3.wireOp",EDGE,"E7")])],"isStart":true}),makeQuery(id+"F4.opExtrude","CAP_FACE",FACE,{"disambiguationData":[OSD([sQuery(id+"F3.wireOp",EDGE,"E6.1"),sQuery(id+"F3.wireOp",EDGE,"E8")])],"isStart":true})]});Q34=makeQuery(id+"F10.opFillet","BLEND_EDGE",EDGE,{"blendedFrom":[makeQuery(id+"F9.boolean.opBoolean","INTERSECT",EDGE,{"derivedFrom":[subQ0,makeQuery(id+"F9.opExtrude","SWEPT_FACE",FACE,{"disambiguationData":[OSD([sQuery(id+"F8.wireOp",EDGE,"E11.1.0.0")])]})]}),makeQuery(id+"F9.boolean.opBoolean","INTERSECT",EDGE,{"derivedFrom":[subQ0,makeQuery(id+"F9.opExtrude","SWEPT_FACE",FACE,{"disambiguationData":[OSD([sQuery(id+"F8.wireOp",EDGE,"E11.1.0.2")])]})]})],"blendedInto":[]});}
            var Q35;
            {var subQ0=makeQuery(id+"F4.boolean.opBoolean","MERGE",FACE,{"derivedFrom":[makeQuery(id+"F1.opExtrude","CAP_FACE",FACE,{"disambiguationData":[OSD([sQuery(id+"F0.wireOp",EDGE,"E0.bottom"),sQuery(id+"F0.wireOp",EDGE,"E0.top"),sQuery(id+"F0.wireOp",EDGE,"E0.left"),sQuery(id+"F0.wireOp",EDGE,"E0.right"),sQuery(id+"F0.wireOp",EDGE,"E4"),sQuery(id+"F0.wireOp",EDGE,"E5")])],"isStart":false}),makeQuery(id+"F4.opExtrude","CAP_FACE",FACE,{"disambiguationData":[OSD([sQuery(id+"F3.wireOp",EDGE,"E6.0"),sQuery(id+"F3.wireOp",EDGE,"E7")])],"isStart":true}),makeQuery(id+"F4.opExtrude","CAP_FACE",FACE,{"disambiguationData":[OSD([sQuery(id+"F3.wireOp",EDGE,"E6.1"),sQuery(id+"F3.wireOp",EDGE,"E8")])],"isStart":true})]});Q35=makeQuery(id+"F10.opFillet","BLEND_EDGE",EDGE,{"blendedFrom":[makeQuery(id+"F9.boolean.opBoolean","INTERSECT",EDGE,{"derivedFrom":[subQ0,makeQuery(id+"F9.opExtrude","SWEPT_FACE",FACE,{"disambiguationData":[OSD([sQuery(id+"F8.wireOp",EDGE,"E11.1.0.0")])]})]}),makeQuery(id+"F9.boolean.opBoolean","INTERSECT",EDGE,{"derivedFrom":[subQ0,makeQuery(id+"F9.opExtrude","SWEPT_FACE",FACE,{"disambiguationData":[OSD([sQuery(id+"F8.wireOp",EDGE,"E11.1.0.4")])]})]})],"blendedInto":[]});}
            var Q36;
            {var subQ0=makeQuery(id+"F4.boolean.opBoolean","MERGE",FACE,{"derivedFrom":[makeQuery(id+"F1.opExtrude","CAP_FACE",FACE,{"disambiguationData":[OSD([sQuery(id+"F0.wireOp",EDGE,"E0.bottom"),sQuery(id+"F0.wireOp",EDGE,"E0.top"),sQuery(id+"F0.wireOp",EDGE,"E0.left"),sQuery(id+"F0.wireOp",EDGE,"E0.right"),sQuery(id+"F0.wireOp",EDGE,"E4"),sQuery(id+"F0.wireOp",EDGE,"E5")])],"isStart":false}),makeQuery(id+"F4.opExtrude","CAP_FACE",FACE,{"disambiguationData":[OSD([sQuery(id+"F3.wireOp",EDGE,"E6.0"),sQuery(id+"F3.wireOp",EDGE,"E7")])],"isStart":true}),makeQuery(id+"F4.opExtrude","CAP_FACE",FACE,{"disambiguationData":[OSD([sQuery(id+"F3.wireOp",EDGE,"E6.1"),sQuery(id+"F3.wireOp",EDGE,"E8")])],"isStart":true})]});Q36=makeQuery(id+"F10.opFillet","BLEND_EDGE",EDGE,{"blendedFrom":[makeQuery(id+"F9.boolean.opBoolean","INTERSECT",EDGE,{"derivedFrom":[subQ0,makeQuery(id+"F9.opExtrude","SWEPT_FACE",FACE,{"disambiguationData":[OSD([sQuery(id+"F8.wireOp",EDGE,"E10.bottom")])]})]}),makeQuery(id+"F9.boolean.opBoolean","INTERSECT",EDGE,{"derivedFrom":[subQ0,makeQuery(id+"F9.opExtrude","SWEPT_FACE",FACE,{"disambiguationData":[OSD([sQuery(id+"F8.wireOp",EDGE,"E10.left")])]})]})],"blendedInto":[]});}
            var Q37;
            {var subQ0=makeQuery(id+"F4.boolean.opBoolean","MERGE",FACE,{"derivedFrom":[makeQuery(id+"F1.opExtrude","CAP_FACE",FACE,{"disambiguationData":[OSD([sQuery(id+"F0.wireOp",EDGE,"E0.bottom"),sQuery(id+"F0.wireOp",EDGE,"E0.top"),sQuery(id+"F0.wireOp",EDGE,"E0.left"),sQuery(id+"F0.wireOp",EDGE,"E0.right"),sQuery(id+"F0.wireOp",EDGE,"E4"),sQuery(id+"F0.wireOp",EDGE,"E5")])],"isStart":false}),makeQuery(id+"F4.opExtrude","CAP_FACE",FACE,{"disambiguationData":[OSD([sQuery(id+"F3.wireOp",EDGE,"E6.0"),sQuery(id+"F3.wireOp",EDGE,"E7")])],"isStart":true}),makeQuery(id+"F4.opExtrude","CAP_FACE",FACE,{"disambiguationData":[OSD([sQuery(id+"F3.wireOp",EDGE,"E6.1"),sQuery(id+"F3.wireOp",EDGE,"E8")])],"isStart":true})]});Q37=makeQuery(id+"F10.opFillet","BLEND_EDGE",EDGE,{"blendedFrom":[makeQuery(id+"F9.boolean.opBoolean","INTERSECT",EDGE,{"derivedFrom":[subQ0,makeQuery(id+"F9.opExtrude","SWEPT_FACE",FACE,{"disambiguationData":[OSD([sQuery(id+"F8.wireOp",EDGE,"E10.top")])]})]}),makeQuery(id+"F9.boolean.opBoolean","INTERSECT",EDGE,{"derivedFrom":[subQ0,makeQuery(id+"F9.opExtrude","SWEPT_FACE",FACE,{"disambiguationData":[OSD([sQuery(id+"F8.wireOp",EDGE,"E10.left")])]})]})],"blendedInto":[]});}
            var Q38;
            {var subQ0=makeQuery(id+"F4.boolean.opBoolean","MERGE",FACE,{"derivedFrom":[makeQuery(id+"F1.opExtrude","CAP_FACE",FACE,{"disambiguationData":[OSD([sQuery(id+"F0.wireOp",EDGE,"E0.bottom"),sQuery(id+"F0.wireOp",EDGE,"E0.top"),sQuery(id+"F0.wireOp",EDGE,"E0.left"),sQuery(id+"F0.wireOp",EDGE,"E0.right"),sQuery(id+"F0.wireOp",EDGE,"E4"),sQuery(id+"F0.wireOp",EDGE,"E5")])],"isStart":false}),makeQuery(id+"F4.opExtrude","CAP_FACE",FACE,{"disambiguationData":[OSD([sQuery(id+"F3.wireOp",EDGE,"E6.0"),sQuery(id+"F3.wireOp",EDGE,"E7")])],"isStart":true}),makeQuery(id+"F4.opExtrude","CAP_FACE",FACE,{"disambiguationData":[OSD([sQuery(id+"F3.wireOp",EDGE,"E6.1"),sQuery(id+"F3.wireOp",EDGE,"E8")])],"isStart":true})]});Q38=makeQuery(id+"F10.opFillet","BLEND_EDGE",EDGE,{"blendedFrom":[makeQuery(id+"F9.boolean.opBoolean","INTERSECT",EDGE,{"derivedFrom":[subQ0,makeQuery(id+"F9.opExtrude","SWEPT_FACE",FACE,{"disambiguationData":[OSD([sQuery(id+"F8.wireOp",EDGE,"E10.top")])]})]}),makeQuery(id+"F9.boolean.opBoolean","INTERSECT",EDGE,{"derivedFrom":[subQ0,makeQuery(id+"F9.opExtrude","SWEPT_FACE",FACE,{"disambiguationData":[OSD([sQuery(id+"F8.wireOp",EDGE,"E10.right")])]})]})],"blendedInto":[]});}
            var Q39;
            {var subQ0=makeQuery(id+"F4.boolean.opBoolean","MERGE",FACE,{"derivedFrom":[makeQuery(id+"F1.opExtrude","CAP_FACE",FACE,{"disambiguationData":[OSD([sQuery(id+"F0.wireOp",EDGE,"E0.bottom"),sQuery(id+"F0.wireOp",EDGE,"E0.top"),sQuery(id+"F0.wireOp",EDGE,"E0.left"),sQuery(id+"F0.wireOp",EDGE,"E0.right"),sQuery(id+"F0.wireOp",EDGE,"E4"),sQuery(id+"F0.wireOp",EDGE,"E5")])],"isStart":false}),makeQuery(id+"F4.opExtrude","CAP_FACE",FACE,{"disambiguationData":[OSD([sQuery(id+"F3.wireOp",EDGE,"E6.0"),sQuery(id+"F3.wireOp",EDGE,"E7")])],"isStart":true}),makeQuery(id+"F4.opExtrude","CAP_FACE",FACE,{"disambiguationData":[OSD([sQuery(id+"F3.wireOp",EDGE,"E6.1"),sQuery(id+"F3.wireOp",EDGE,"E8")])],"isStart":true})]});Q39=makeQuery(id+"F10.opFillet","BLEND_EDGE",EDGE,{"blendedFrom":[makeQuery(id+"F9.boolean.opBoolean","INTERSECT",EDGE,{"derivedFrom":[subQ0,makeQuery(id+"F9.opExtrude","SWEPT_FACE",FACE,{"disambiguationData":[OSD([sQuery(id+"F8.wireOp",EDGE,"E10.bottom")])]})]}),makeQuery(id+"F9.boolean.opBoolean","INTERSECT",EDGE,{"derivedFrom":[subQ0,makeQuery(id+"F9.opExtrude","SWEPT_FACE",FACE,{"disambiguationData":[OSD([sQuery(id+"F8.wireOp",EDGE,"E10.right")])]})]})],"blendedInto":[]});}
            fillet(context, id + "F13", {"entities" : qUnion([Q0, Q1, Q2, Q3, Q4, Q5, Q6, Q7, Q8, Q9, Q10, Q11, Q12, Q13, Q14, Q15, Q16, Q17, Q18, Q19, Q20, Q21, Q22, Q23, Q24, Q25, Q26, Q27, Q28, Q29, Q30, Q31, Q32, Q33, Q34, Q35, Q36, Q37, Q38, Q39]), "radius" : 0.2 * mm, "tangentPropagation" : true, "allowEdgeOverflow" : false});
        }
    });
